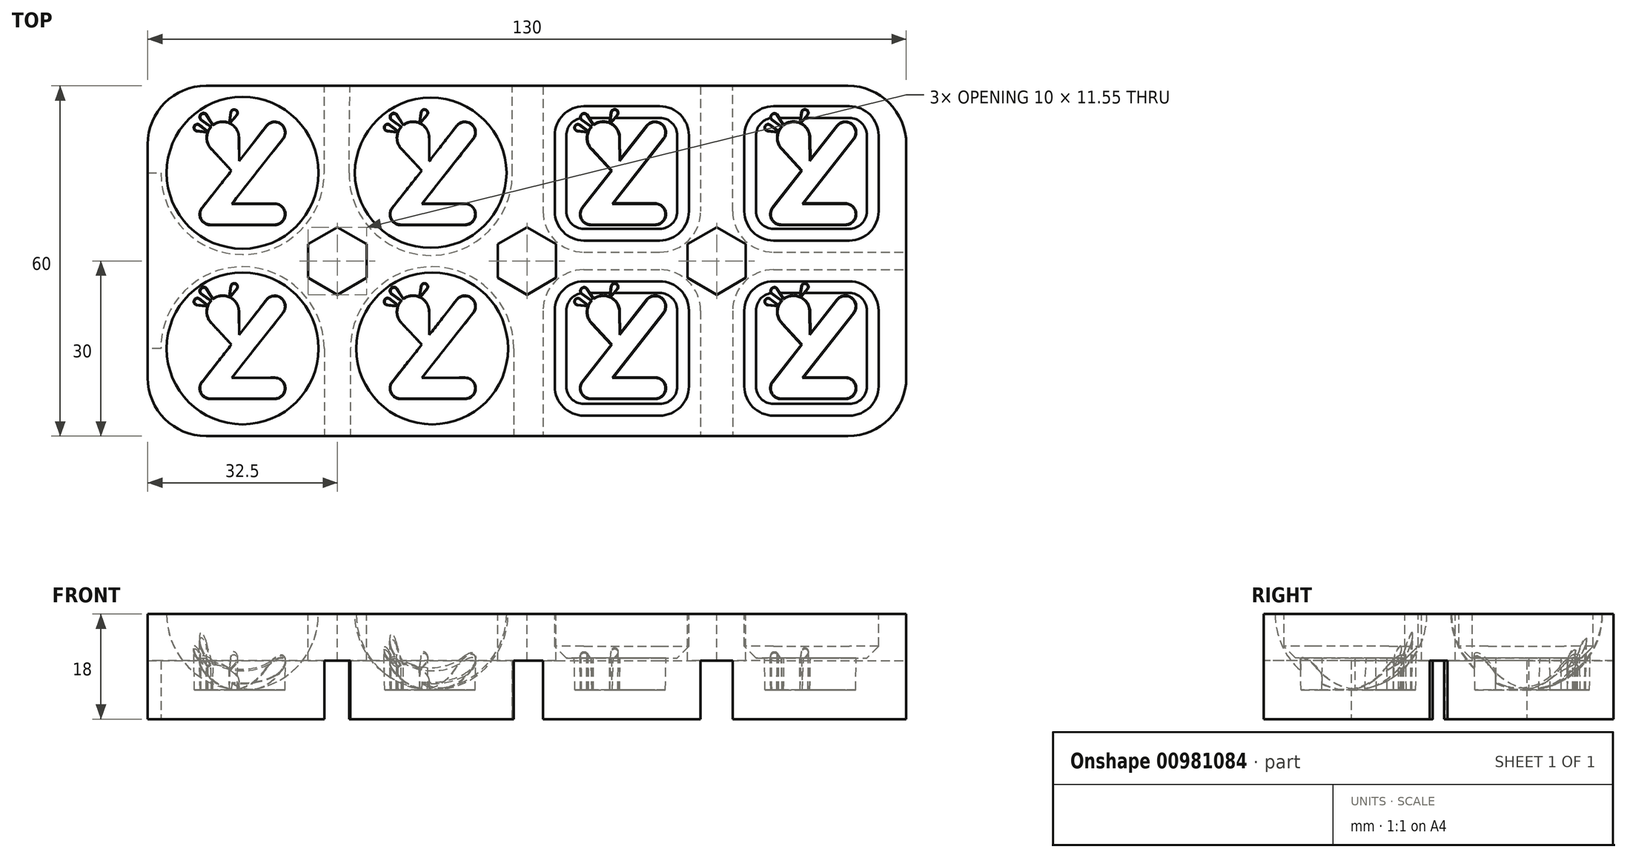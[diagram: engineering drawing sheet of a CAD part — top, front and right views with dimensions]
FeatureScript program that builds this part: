
annotation { "Feature Type Name" : "Feature", "Feature Type Description" : "" }
export const myFeature = defineFeature(function(context is Context, id is Id, definition is map)
    precondition{}
    {
        {
            var Q0;
            Q0=qCreatedBy(makeId("Top.planeOp"),FACE);
            var sketch = newSketch(context, id + "F0", { "sketchPlane" : qUnion([Q0])});
            skLineSegment(sketch, "E0.bottom", {"start": v(-55, 30) * mm, "end": v(55, 30) * mm});
            skLineSegment(sketch, "E0.top", {"start": v(-55, -30) * mm, "end": v(55, -30) * mm});
            skLineSegment(sketch, "E0.left", {"start": v(-65, 20) * mm, "end": v(-65, -20) * mm});
            skLineSegment(sketch, "E0.right", {"start": v(65, 20) * mm, "end": v(65, -20) * mm});
            skPoint(sketch, "E1", {"position": v(0, 30) * mm});
            skPoint(sketch, "E2", {"position": v(65, 0) * mm});
            skPoint(sketch, "E3.visualSharp", {"position": v(65, 30) * mm});
            skArc(sketch, "E3.filletArc", {"start": v(65, 20) * mm, "mid": v(62.07, 27.07) * mm, "end": v(55, 30) * mm});
            skPoint(sketch, "E4.visualSharp", {"position": v(65, -30) * mm});
            skArc(sketch, "E4.filletArc", {"start": v(55, -30) * mm, "mid": v(62.07, -27.07) * mm, "end": v(65, -20) * mm});
            skPoint(sketch, "E5.visualSharp", {"position": v(-65, -30) * mm});
            skArc(sketch, "E5.filletArc", {"start": v(-65, -20) * mm, "mid": v(-62.07, -27.07) * mm, "end": v(-55, -30) * mm});
            skPoint(sketch, "E6.visualSharp", {"position": v(-65, 30) * mm});
            skArc(sketch, "E6.filletArc", {"start": v(-55, 30) * mm, "mid": v(-62.07, 27.07) * mm, "end": v(-65, 20) * mm});
            skSolve(sketch);
        }
        {
            var Q0;
            Q0 = qSketchRegion(id + "F0", true);
            extrude(context, id + "F1", {"entities" : qUnion([Q0]), "depth" : 18 * mm, "offsetDistance" : 25 * mm});
        }
        {
            var Q0;
            Q0=makeQuery(id+"F1.opExtrude","CAP_FACE",FACE,{"disambiguationData":[OSD([sQuery(id+"F0.wireOp",EDGE,"E0.bottom"),sQuery(id+"F0.wireOp",EDGE,"E0.top"),sQuery(id+"F0.wireOp",EDGE,"E0.left"),sQuery(id+"F0.wireOp",EDGE,"E0.right"),sQuery(id+"F0.wireOp",EDGE,"E3.filletArc"),sQuery(id+"F0.wireOp",EDGE,"E4.filletArc"),sQuery(id+"F0.wireOp",EDGE,"E5.filletArc"),sQuery(id+"F0.wireOp",EDGE,"E6.filletArc")])],"isStart":false});
            var sketch = newSketch(context, id + "F2", { "sketchPlane" : qUnion([Q0])});
            skLineSegment(sketch, "E7", {"start": v(-65, 0) * mm, "end": v(65, 0) * mm, "construction": true});
            skLineSegment(sketch, "E8", {"start": v(0, 30) * mm, "end": v(0, -30) * mm, "construction": true});
            skLineSegment(sketch, "E9", {"start": v(-65, 20) * mm, "end": v(0, 20) * mm, "construction": true});
            skLineSegment(sketch, "E10", {"start": v(-32.5, 30) * mm, "end": v(-32.5, -30) * mm, "construction": true});
            skPoint(sketch, "E10.startSnap0", {"position": v(-32.5, 20) * mm});
            skLineSegment(sketch, "E11", {"start": v(-32.5, 30) * mm, "end": v(-32.5, 0) * mm});
            skPoint(sketch, "E12.startSnap0", {"position": v(-32.5, 15) * mm});
            skCircle(sketch, "E13", {"center": v(-48.75, 15) * mm, "radius": 12.5 * mm, "construction": true});
            skLineSegment(sketch, "E14", {"start": v(-65, 15) * mm, "end": v(-32.5, 15) * mm, "construction": true});
            skLineSegment(sketch, "E15", {"start": v(-61.25, 0) * mm, "end": v(-61.25, 15) * mm, "construction": true});
            skCircle(sketch, "E16.MirrorC", {"center": v(-73.75, 15) * mm, "radius": 12.5 * mm, "construction": true});
            skLineSegment(sketch, "E17", {"start": v(-79.25, 8) * mm, "end": v(-68.25, 8) * mm, "construction": true});
            skLineSegment(sketch, "E18", {"start": v(-68.25, 8) * mm, "end": v(-79.25, 22) * mm, "construction": true});
            skPoint(sketch, "E19", {"position": v(-73.75, 8) * mm});
            skLineSegment(sketch, "E20", {"start": v(-77.68, 23.24) * mm, "end": v(-80.82, 20.76) * mm, "construction": true});
            skLineSegment(sketch, "E21", {"start": v(-80.82, 20.76) * mm, "end": v(-72.36, 10) * mm, "construction": true});
            skLineSegment(sketch, "E22", {"start": v(-72.36, 10) * mm, "end": v(-79.25, 10) * mm, "construction": true});
            skArc(sketch, "E23", {"start": v(-68.25, 6) * mm, "mid": v(-66.45, 7.13) * mm, "end": v(-66.68, 9.24) * mm, "construction": true});
            skLineSegment(sketch, "E24", {"start": v(-79.25, 6) * mm, "end": v(-68.25, 6) * mm, "construction": true});
            skLineSegment(sketch, "E25", {"start": v(-73.13, 14.21) * mm, "end": v(-70.01, 22) * mm, "construction": true});
            skArc(sketch, "E26", {"start": v(-69.08, 21.63) * mm, "mid": v(-69.64, 22.93) * mm, "end": v(-70.94, 22.37) * mm, "construction": true});
            skLineSegment(sketch, "E27", {"start": v(-72.99, 17.27) * mm, "end": v(-71.56, 15.45) * mm, "construction": true});
            skLineSegment(sketch, "E28", {"start": v(-71.56, 15.45) * mm, "end": v(-66.68, 9.24) * mm, "construction": true});
            skLineSegment(sketch, "E29", {"start": v(-70.94, 22.37) * mm, "end": v(-72.99, 17.27) * mm, "construction": true});
            skLineSegment(sketch, "E30", {"start": v(-69.08, 21.63) * mm, "end": v(-71.56, 15.45) * mm, "construction": true});
            skLineSegment(sketch, "E31", {"start": v(-70.94, 22.37) * mm, "end": v(-69.08, 21.63) * mm, "construction": true});
            skLineSegment(sketch, "E32", {"start": v(-71.56, 15.45) * mm, "end": v(-68.3, 18.97) * mm, "construction": true});
            skPoint(sketch, "E32.endSnap0", {"position": v(-72.27, 16.36) * mm});
            skArc(sketch, "E33", {"start": v(-68.3, 18.97) * mm, "mid": v(-67.51, 20.33) * mm, "end": v(-67.54, 21.9) * mm, "construction": true});
            skLineSegment(sketch, "E34", {"start": v(-73.35, 21) * mm, "end": v(-68.3, 18.97) * mm, "construction": true});
            skLineSegment(sketch, "E35", {"start": v(-73.35, 21) * mm, "end": v(-73.4, 17.78) * mm, "construction": true});
            skLineSegment(sketch, "E36", {"start": v(-73.4, 17.78) * mm, "end": v(-72.99, 17.27) * mm, "construction": true});
            skLineSegment(sketch, "E37", {"start": v(-73.4, 17.78) * mm, "end": v(-76.54, 15.31) * mm, "construction": true});
            skLineSegment(sketch, "E38", {"start": v(-73.4, 17.78) * mm, "end": v(-77.68, 23.24) * mm, "construction": true});
            skArc(sketch, "E39", {"start": v(-77.68, 23.24) * mm, "mid": v(-80.49, 23.57) * mm, "end": v(-80.82, 20.76) * mm, "construction": true});
            skLineSegment(sketch, "E40", {"start": v(-80.82, 20.76) * mm, "end": v(-77.68, 23.24) * mm, "construction": true});
            skLineSegment(sketch, "E41", {"start": v(-80.82, 20.76) * mm, "end": v(-76.54, 15.31) * mm, "construction": true});
            skLineSegment(sketch, "E42", {"start": v(-76.54, 15.31) * mm, "end": v(-72.36, 10) * mm, "construction": true});
            skLineSegment(sketch, "E43", {"start": v(-71.87, 23.63) * mm, "end": v(-72.9, 24.88) * mm, "construction": true});
            skLineSegment(sketch, "E44", {"start": v(-71.33, 23.88) * mm, "end": v(-71.58, 25.47) * mm, "construction": true});
            skArc(sketch, "E45", {"start": v(-71.58, 25.47) * mm, "mid": v(-72.63, 26.04) * mm, "end": v(-72.9, 24.88) * mm, "construction": true});
            skLineSegment(sketch, "E46", {"start": v(-72.32, 25.35) * mm, "end": v(-70.38, 21.07) * mm, "construction": true});
            skPoint(sketch, "E47", {"position": v(-71.6, 23.77) * mm});
            skLineSegment(sketch, "E48", {"start": v(-72.9, 24.88) * mm, "end": v(-71.58, 25.47) * mm, "construction": true});
            skLineSegment(sketch, "E49.MirrorCS", {"start": v(-65.94, 22.08) * mm, "end": v(-66.48, 23.43) * mm, "construction": true});
            skLineSegment(sketch, "E50.MirrorCS", {"start": v(-66.02, 22.83) * mm, "end": v(-70.38, 21.07) * mm, "construction": true});
            skLineSegment(sketch, "E51.MirrorCS", {"start": v(-67.76, 22.45) * mm, "end": v(-66.48, 23.43) * mm, "construction": true});
            skLineSegment(sketch, "E52.MirrorCS", {"start": v(-67.54, 21.9) * mm, "end": v(-65.94, 22.08) * mm, "construction": true});
            skArc(sketch, "E53.MirrorCS", {"start": v(-66.48, 23.43) * mm, "mid": v(-65.33, 23.1) * mm, "end": v(-65.94, 22.08) * mm, "construction": true});
            skArc(sketch, "E54", {"start": v(-71.87, 23.63) * mm, "mid": v(-72.97, 22.52) * mm, "end": v(-73.35, 21) * mm, "construction": true});
            skArc(sketch, "E55", {"start": v(-71.33, 23.88) * mm, "mid": v(-71.6, 23.77) * mm, "end": v(-71.87, 23.63) * mm, "construction": true});
            skArc(sketch, "E56", {"start": v(-68.74, 23.54) * mm, "mid": v(-70, 24) * mm, "end": v(-71.33, 23.88) * mm, "construction": true});
            skArc(sketch, "E57", {"start": v(-68.08, 22.94) * mm, "mid": v(-68.39, 23.26) * mm, "end": v(-68.74, 23.54) * mm, "construction": true});
            skArc(sketch, "E58", {"start": v(-67.76, 22.45) * mm, "mid": v(-67.9, 22.7) * mm, "end": v(-68.08, 22.94) * mm, "construction": true});
            skArc(sketch, "E59", {"start": v(-67.54, 21.9) * mm, "mid": v(-67.63, 22.18) * mm, "end": v(-67.76, 22.45) * mm, "construction": true});
            skArc(sketch, "E60", {"start": v(-79.25, 10) * mm, "mid": v(-81.25, 8) * mm, "end": v(-79.25, 6) * mm, "construction": true});
            skLineSegment(sketch, "E61", {"start": v(-70.01, 22) * mm, "end": v(-66.8, 24.9) * mm, "construction": true});
            skPoint(sketch, "E62", {"position": v(-68.5, 23.36) * mm});
            skArc(sketch, "E63", {"start": v(-66.5, 24.1) * mm, "mid": v(-66.56, 25.22) * mm, "end": v(-67.69, 25.17) * mm, "construction": true});
            skLineSegment(sketch, "E64", {"start": v(-68.74, 23.54) * mm, "end": v(-68.08, 22.94) * mm, "construction": true});
            skLineSegment(sketch, "E65", {"start": v(-67.69, 25.17) * mm, "end": v(-66.5, 24.1) * mm, "construction": true});
            skLineSegment(sketch, "E66", {"start": v(-68.74, 23.54) * mm, "end": v(-67.69, 25.17) * mm, "construction": true});
            skLineSegment(sketch, "E67", {"start": v(-66.5, 24.1) * mm, "end": v(-68.08, 22.94) * mm, "construction": true});
            skLineSegment(sketch, "E68.MirrorCS", {"start": v(-51.56, 22.37) * mm, "end": v(-53.42, 21.63) * mm, "construction": true});
            skArc(sketch, "E69.MirrorCS", {"start": v(-51.17, 23.88) * mm, "mid": v(-50.9, 23.77) * mm, "end": v(-50.63, 23.63) * mm, "construction": true});
            skLineSegment(sketch, "E70.MirrorCS", {"start": v(-50.18, 25.35) * mm, "end": v(-52.12, 21.07) * mm, "construction": true});
            skLineSegment(sketch, "E71.MirrorCS", {"start": v(-51.17, 23.88) * mm, "end": v(-50.92, 25.47) * mm});
            skLineSegment(sketch, "E72.MirrorCS", {"start": v(-49.6, 24.88) * mm, "end": v(-50.92, 25.47) * mm, "construction": true});
            skLineSegment(sketch, "E73.MirrorCS", {"start": v(-54.74, 22.45) * mm, "end": v(-56.02, 23.43) * mm});
            skArc(sketch, "E74.MirrorCS", {"start": v(-54.42, 22.94) * mm, "mid": v(-54.11, 23.26) * mm, "end": v(-53.76, 23.54) * mm, "construction": true});
            skLineSegment(sketch, "E75.MirrorCS", {"start": v(-54.96, 21.9) * mm, "end": v(-56.56, 22.08) * mm});
            skLineSegment(sketch, "E76.MirrorCS", {"start": v(-53.76, 23.54) * mm, "end": v(-54.81, 25.17) * mm});
            skArc(sketch, "E77.MirrorCS", {"start": v(-54.74, 22.45) * mm, "mid": v(-54.6, 22.7) * mm, "end": v(-54.42, 22.94) * mm});
            skArc(sketch, "E78.MirrorCS", {"start": v(-50.92, 25.47) * mm, "mid": v(-49.87, 26.04) * mm, "end": v(-49.6, 24.88) * mm});
            skLineSegment(sketch, "E79.MirrorCS", {"start": v(-44.82, 23.24) * mm, "end": v(-41.68, 20.76) * mm, "construction": true});
            skArc(sketch, "E80.MirrorCS", {"start": v(-53.76, 23.54) * mm, "mid": v(-52.5, 24) * mm, "end": v(-51.17, 23.88) * mm});
            skLineSegment(sketch, "E81.MirrorCS", {"start": v(-56, 24.1) * mm, "end": v(-54.42, 22.94) * mm});
            skArc(sketch, "E82.MirrorCS", {"start": v(-54.96, 21.9) * mm, "mid": v(-54.87, 22.18) * mm, "end": v(-54.74, 22.45) * mm, "construction": true});
            skLineSegment(sketch, "E83.MirrorCS", {"start": v(-49.51, 17.27) * mm, "end": v(-50.94, 15.45) * mm, "construction": true});
            skLineSegment(sketch, "E84.MirrorCS", {"start": v(-50.63, 23.63) * mm, "end": v(-49.6, 24.88) * mm});
            skLineSegment(sketch, "E85.MirrorCS", {"start": v(-53.76, 23.54) * mm, "end": v(-54.42, 22.94) * mm, "construction": true});
            skArc(sketch, "E86.MirrorCS", {"start": v(-53.42, 21.63) * mm, "mid": v(-52.86, 22.93) * mm, "end": v(-51.56, 22.37) * mm, "construction": true});
            skLineSegment(sketch, "E87.MirrorCS", {"start": v(-56.48, 22.83) * mm, "end": v(-52.12, 21.07) * mm, "construction": true});
            skArc(sketch, "E88.MirrorCS", {"start": v(-56.02, 23.43) * mm, "mid": v(-57.17, 23.1) * mm, "end": v(-56.56, 22.08) * mm});
            skLineSegment(sketch, "E89.MirrorCS", {"start": v(-56.56, 22.08) * mm, "end": v(-56.02, 23.43) * mm, "construction": true});
            skLineSegment(sketch, "E90.MirrorCS", {"start": v(-41.68, 20.76) * mm, "end": v(-44.82, 23.24) * mm, "construction": true});
            skLineSegment(sketch, "E91.MirrorCS", {"start": v(-49.1, 17.78) * mm, "end": v(-49.51, 17.27) * mm, "construction": true});
            skLineSegment(sketch, "E92.MirrorCS", {"start": v(-54.81, 25.17) * mm, "end": v(-56, 24.1) * mm, "construction": true});
            skLineSegment(sketch, "E93.MirrorCS", {"start": v(-49.1, 17.78) * mm, "end": v(-45.96, 15.31) * mm, "construction": true});
            skLineSegment(sketch, "E94.MirrorCS", {"start": v(-52.49, 22) * mm, "end": v(-55.7, 24.9) * mm, "construction": true});
            skLineSegment(sketch, "E95.MirrorCS", {"start": v(-49.15, 21) * mm, "end": v(-49.1, 17.78) * mm});
            skArc(sketch, "E96.MirrorCS", {"start": v(-50.63, 23.63) * mm, "mid": v(-49.53, 22.52) * mm, "end": v(-49.15, 21) * mm});
            skLineSegment(sketch, "E97.MirrorCS", {"start": v(-51.56, 22.37) * mm, "end": v(-49.51, 17.27) * mm, "construction": true});
            skArc(sketch, "E98.MirrorCS", {"start": v(-54.2, 18.97) * mm, "mid": v(-54.99, 20.33) * mm, "end": v(-54.96, 21.9) * mm});
            skArc(sketch, "E99.MirrorCS", {"start": v(-56, 24.1) * mm, "mid": v(-55.94, 25.22) * mm, "end": v(-54.81, 25.17) * mm});
            skPoint(sketch, "E100.MirrorP", {"position": v(-50.9, 23.77) * mm});
            skLineSegment(sketch, "E101.MirrorCS", {"start": v(-41.68, 20.76) * mm, "end": v(-45.96, 15.31) * mm});
            skLineSegment(sketch, "E102.MirrorCS", {"start": v(-45.96, 15.31) * mm, "end": v(-50.14, 10) * mm});
            skLineSegment(sketch, "E103.MirrorCS", {"start": v(-49.15, 21) * mm, "end": v(-54.2, 18.97) * mm, "construction": true});
            skLineSegment(sketch, "E104.MirrorCS", {"start": v(-53.42, 21.63) * mm, "end": v(-50.94, 15.45) * mm, "construction": true});
            skLineSegment(sketch, "E105.MirrorCS", {"start": v(-50.94, 15.45) * mm, "end": v(-55.82, 9.24) * mm});
            skLineSegment(sketch, "E106.MirrorCS", {"start": v(-50.94, 15.45) * mm, "end": v(-54.2, 18.97) * mm});
            skLineSegment(sketch, "E107.MirrorCS", {"start": v(-41.68, 20.76) * mm, "end": v(-50.14, 10) * mm, "construction": true});
            skArc(sketch, "E108.MirrorCS", {"start": v(-43.25, 10) * mm, "mid": v(-41.25, 8) * mm, "end": v(-43.25, 6) * mm});
            skPoint(sketch, "E109.MirrorP", {"position": v(-50.23, 16.36) * mm});
            skArc(sketch, "E110.MirrorCS", {"start": v(-54.25, 6) * mm, "mid": v(-56.05, 7.13) * mm, "end": v(-55.82, 9.24) * mm});
            skLineSegment(sketch, "E111.MirrorCS", {"start": v(-54.25, 8) * mm, "end": v(-43.25, 22) * mm, "construction": true});
            skLineSegment(sketch, "E112.MirrorCS", {"start": v(-49.1, 17.78) * mm, "end": v(-44.82, 23.24) * mm});
            skPoint(sketch, "E113.MirrorP", {"position": v(-54, 23.36) * mm});
            skLineSegment(sketch, "E114.MirrorCS", {"start": v(-43.25, 6) * mm, "end": v(-54.25, 6) * mm});
            skPoint(sketch, "E115.MirrorP", {"position": v(-48.75, 8) * mm});
            skLineSegment(sketch, "E116.MirrorCS", {"start": v(-49.37, 14.21) * mm, "end": v(-52.49, 22) * mm, "construction": true});
            skArc(sketch, "E117.MirrorCS", {"start": v(-44.82, 23.24) * mm, "mid": v(-42.01, 23.57) * mm, "end": v(-41.68, 20.76) * mm});
            skLineSegment(sketch, "E118.MirrorCS", {"start": v(-50.14, 10) * mm, "end": v(-43.25, 10) * mm});
            skLineSegment(sketch, "E119.MirrorCS", {"start": v(-43.25, 8) * mm, "end": v(-54.25, 8) * mm, "construction": true});
            skLineSegment(sketch, "E120.0.1.0", {"start": v(-54.25, -21.8) * mm, "end": v(-43.25, -7.8) * mm, "construction": true});
            skLineSegment(sketch, "E120.0.1.1", {"start": v(-50.94, -14.35) * mm, "end": v(-55.82, -20.56) * mm});
            skPoint(sketch, "E120.0.1.2", {"position": v(-50.9, -6.03) * mm});
            skPoint(sketch, "E120.0.1.3", {"position": v(-50.23, -13.44) * mm});
            skArc(sketch, "E120.0.1.4", {"start": v(-44.82, -6.56) * mm, "mid": v(-42.01, -6.23) * mm, "end": v(-41.68, -9.04) * mm});
            skPoint(sketch, "E120.0.1.5", {"position": v(-48.75, -21.8) * mm});
            skLineSegment(sketch, "E120.0.1.6", {"start": v(-41.68, -9.04) * mm, "end": v(-50.14, -19.8) * mm, "construction": true});
            skPoint(sketch, "E120.0.1.7", {"position": v(-48.75, -14.8) * mm});
            skArc(sketch, "E120.0.1.8", {"start": v(-43.25, -19.8) * mm, "mid": v(-41.25, -21.8) * mm, "end": v(-43.25, -23.8) * mm});
            skPoint(sketch, "E120.0.1.9", {"position": v(-54, -6.44) * mm});
            skLineSegment(sketch, "E120.0.1.10", {"start": v(-49.1, -12.02) * mm, "end": v(-44.82, -6.56) * mm});
            skLineSegment(sketch, "E120.0.1.11", {"start": v(-41.68, -9.04) * mm, "end": v(-45.96, -14.49) * mm});
            skLineSegment(sketch, "E120.0.1.12", {"start": v(-43.25, -21.8) * mm, "end": v(-54.25, -21.8) * mm, "construction": true});
            skLineSegment(sketch, "E120.0.1.13", {"start": v(-43.25, -23.8) * mm, "end": v(-54.25, -23.8) * mm});
            skLineSegment(sketch, "E120.0.1.14", {"start": v(-50.14, -19.8) * mm, "end": v(-43.25, -19.8) * mm});
            skLineSegment(sketch, "E120.0.1.15", {"start": v(-45.96, -14.49) * mm, "end": v(-50.14, -19.8) * mm});
            skArc(sketch, "E120.0.1.16", {"start": v(-54.25, -23.8) * mm, "mid": v(-56.05, -22.67) * mm, "end": v(-55.82, -20.56) * mm});
            skLineSegment(sketch, "E120.0.1.17", {"start": v(-50.94, -14.35) * mm, "end": v(-54.2, -10.83) * mm});
            skLineSegment(sketch, "E120.0.1.18", {"start": v(-49.15, -8.8) * mm, "end": v(-54.2, -10.83) * mm, "construction": true});
            skLineSegment(sketch, "E120.0.1.19", {"start": v(-49.1, -12.02) * mm, "end": v(-45.96, -14.49) * mm, "construction": true});
            skLineSegment(sketch, "E120.0.1.20", {"start": v(-53.42, -8.17) * mm, "end": v(-50.94, -14.35) * mm, "construction": true});
            skArc(sketch, "E120.0.1.21", {"start": v(-54.2, -10.83) * mm, "mid": v(-54.99, -9.47) * mm, "end": v(-54.96, -7.9) * mm});
            skArc(sketch, "E120.0.1.22", {"start": v(-56, -5.7) * mm, "mid": v(-55.94, -4.58) * mm, "end": v(-54.81, -4.63) * mm});
            skArc(sketch, "E120.0.1.23", {"start": v(-56.02, -6.37) * mm, "mid": v(-57.17, -6.7) * mm, "end": v(-56.56, -7.72) * mm});
            skLineSegment(sketch, "E120.0.1.24", {"start": v(-49.15, -8.8) * mm, "end": v(-49.1, -12.02) * mm});
            skLineSegment(sketch, "E120.0.1.25", {"start": v(-44.82, -6.56) * mm, "end": v(-41.68, -9.04) * mm, "construction": true});
            skLineSegment(sketch, "E120.0.1.26", {"start": v(-51.56, -7.43) * mm, "end": v(-49.51, -12.53) * mm, "construction": true});
            skLineSegment(sketch, "E120.0.1.27", {"start": v(-49.37, -15.59) * mm, "end": v(-52.49, -7.8) * mm, "construction": true});
            skArc(sketch, "E120.0.1.28", {"start": v(-50.63, -6.17) * mm, "mid": v(-49.53, -7.28) * mm, "end": v(-49.15, -8.8) * mm});
            skLineSegment(sketch, "E120.0.1.29", {"start": v(-49.51, -12.53) * mm, "end": v(-50.94, -14.35) * mm, "construction": true});
            skLineSegment(sketch, "E120.0.1.30", {"start": v(-41.68, -9.04) * mm, "end": v(-44.82, -6.56) * mm, "construction": true});
            skLineSegment(sketch, "E120.0.1.31", {"start": v(-49.1, -12.02) * mm, "end": v(-49.51, -12.53) * mm, "construction": true});
            skLineSegment(sketch, "E120.0.1.32", {"start": v(-53.76, -6.26) * mm, "end": v(-54.81, -4.63) * mm});
            skLineSegment(sketch, "E120.0.1.33", {"start": v(-54.81, -4.63) * mm, "end": v(-56, -5.7) * mm, "construction": true});
            skLineSegment(sketch, "E120.0.1.34", {"start": v(-52.49, -7.8) * mm, "end": v(-55.7, -4.9) * mm, "construction": true});
            skLineSegment(sketch, "E120.0.1.35", {"start": v(-50.63, -6.17) * mm, "end": v(-49.6, -4.92) * mm});
            skLineSegment(sketch, "E120.0.1.36", {"start": v(-49.6, -4.92) * mm, "end": v(-50.92, -4.33) * mm, "construction": true});
            skLineSegment(sketch, "E120.0.1.37", {"start": v(-50.18, -4.45) * mm, "end": v(-52.12, -8.73) * mm, "construction": true});
            skLineSegment(sketch, "E120.0.1.38", {"start": v(-51.17, -5.92) * mm, "end": v(-50.92, -4.33) * mm});
            skArc(sketch, "E120.0.1.39", {"start": v(-51.17, -5.92) * mm, "mid": v(-50.9, -6.03) * mm, "end": v(-50.63, -6.17) * mm, "construction": true});
            skArc(sketch, "E120.0.1.40", {"start": v(-53.76, -6.26) * mm, "mid": v(-52.5, -5.8) * mm, "end": v(-51.17, -5.92) * mm});
            skArc(sketch, "E120.0.1.41", {"start": v(-50.92, -4.33) * mm, "mid": v(-49.87, -3.76) * mm, "end": v(-49.6, -4.92) * mm});
            skLineSegment(sketch, "E120.0.1.42", {"start": v(-56, -5.7) * mm, "end": v(-54.42, -6.86) * mm});
            skLineSegment(sketch, "E120.0.1.43", {"start": v(-51.56, -7.43) * mm, "end": v(-53.42, -8.17) * mm, "construction": true});
            skLineSegment(sketch, "E120.0.1.44", {"start": v(-56.56, -7.72) * mm, "end": v(-56.02, -6.37) * mm, "construction": true});
            skArc(sketch, "E120.0.1.45", {"start": v(-53.42, -8.17) * mm, "mid": v(-52.86, -6.87) * mm, "end": v(-51.56, -7.43) * mm, "construction": true});
            skLineSegment(sketch, "E120.0.1.46", {"start": v(-56.48, -6.97) * mm, "end": v(-52.12, -8.73) * mm, "construction": true});
            skLineSegment(sketch, "E120.0.1.47", {"start": v(-53.76, -6.26) * mm, "end": v(-54.42, -6.86) * mm, "construction": true});
            skLineSegment(sketch, "E120.0.1.48", {"start": v(-54.96, -7.9) * mm, "end": v(-56.56, -7.72) * mm});
            skArc(sketch, "E120.0.1.49", {"start": v(-54.96, -7.9) * mm, "mid": v(-54.87, -7.62) * mm, "end": v(-54.74, -7.35) * mm, "construction": true});
            skLineSegment(sketch, "E120.0.1.50", {"start": v(-54.74, -7.35) * mm, "end": v(-56.02, -6.37) * mm});
            skArc(sketch, "E120.0.1.51", {"start": v(-54.42, -6.86) * mm, "mid": v(-54.11, -6.54) * mm, "end": v(-53.76, -6.26) * mm, "construction": true});
            skArc(sketch, "E120.0.1.52", {"start": v(-54.74, -7.35) * mm, "mid": v(-54.6, -7.1) * mm, "end": v(-54.42, -6.86) * mm});
            skLineSegment(sketch, "E120.1.0.0", {"start": v(-21.65, 8) * mm, "end": v(-10.65, 22) * mm, "construction": true});
            skLineSegment(sketch, "E120.1.0.1", {"start": v(-18.34, 15.45) * mm, "end": v(-23.22, 9.24) * mm});
            skPoint(sketch, "E120.1.0.2", {"position": v(-18.3, 23.77) * mm});
            skPoint(sketch, "E120.1.0.3", {"position": v(-17.63, 16.36) * mm});
            skArc(sketch, "E120.1.0.4", {"start": v(-12.22, 23.24) * mm, "mid": v(-9.41, 23.57) * mm, "end": v(-9.08, 20.76) * mm});
            skPoint(sketch, "E120.1.0.5", {"position": v(-16.15, 8) * mm});
            skLineSegment(sketch, "E120.1.0.6", {"start": v(-9.08, 20.76) * mm, "end": v(-17.54, 10) * mm, "construction": true});
            skPoint(sketch, "E120.1.0.7", {"position": v(-16.15, 15) * mm});
            skArc(sketch, "E120.1.0.8", {"start": v(-10.65, 10) * mm, "mid": v(-8.65, 8) * mm, "end": v(-10.65, 6) * mm});
            skPoint(sketch, "E120.1.0.9", {"position": v(-21.4, 23.36) * mm});
            skLineSegment(sketch, "E120.1.0.10", {"start": v(-16.5, 17.78) * mm, "end": v(-12.22, 23.24) * mm});
            skLineSegment(sketch, "E120.1.0.11", {"start": v(-9.08, 20.76) * mm, "end": v(-13.36, 15.31) * mm});
            skLineSegment(sketch, "E120.1.0.12", {"start": v(-10.65, 8) * mm, "end": v(-21.65, 8) * mm, "construction": true});
            skLineSegment(sketch, "E120.1.0.13", {"start": v(-10.65, 6) * mm, "end": v(-21.65, 6) * mm});
            skLineSegment(sketch, "E120.1.0.14", {"start": v(-17.54, 10) * mm, "end": v(-10.65, 10) * mm});
            skLineSegment(sketch, "E120.1.0.15", {"start": v(-13.36, 15.31) * mm, "end": v(-17.54, 10) * mm});
            skArc(sketch, "E120.1.0.16", {"start": v(-21.65, 6) * mm, "mid": v(-23.45, 7.13) * mm, "end": v(-23.22, 9.24) * mm});
            skLineSegment(sketch, "E120.1.0.17", {"start": v(-18.34, 15.45) * mm, "end": v(-21.6, 18.97) * mm});
            skLineSegment(sketch, "E120.1.0.18", {"start": v(-16.55, 21) * mm, "end": v(-21.6, 18.97) * mm, "construction": true});
            skLineSegment(sketch, "E120.1.0.19", {"start": v(-16.5, 17.78) * mm, "end": v(-13.36, 15.31) * mm, "construction": true});
            skLineSegment(sketch, "E120.1.0.20", {"start": v(-20.82, 21.63) * mm, "end": v(-18.34, 15.45) * mm, "construction": true});
            skArc(sketch, "E120.1.0.21", {"start": v(-21.6, 18.97) * mm, "mid": v(-22.39, 20.33) * mm, "end": v(-22.36, 21.9) * mm});
            skArc(sketch, "E120.1.0.22", {"start": v(-23.4, 24.1) * mm, "mid": v(-23.34, 25.22) * mm, "end": v(-22.21, 25.17) * mm});
            skArc(sketch, "E120.1.0.23", {"start": v(-23.42, 23.43) * mm, "mid": v(-24.57, 23.1) * mm, "end": v(-23.96, 22.08) * mm});
            skLineSegment(sketch, "E120.1.0.24", {"start": v(-16.55, 21) * mm, "end": v(-16.5, 17.78) * mm});
            skLineSegment(sketch, "E120.1.0.25", {"start": v(-12.22, 23.24) * mm, "end": v(-9.08, 20.76) * mm, "construction": true});
            skLineSegment(sketch, "E120.1.0.26", {"start": v(-18.96, 22.37) * mm, "end": v(-16.91, 17.27) * mm, "construction": true});
            skLineSegment(sketch, "E120.1.0.27", {"start": v(-16.77, 14.21) * mm, "end": v(-19.89, 22) * mm, "construction": true});
            skArc(sketch, "E120.1.0.28", {"start": v(-18.03, 23.63) * mm, "mid": v(-16.93, 22.52) * mm, "end": v(-16.55, 21) * mm});
            skLineSegment(sketch, "E120.1.0.29", {"start": v(-16.91, 17.27) * mm, "end": v(-18.34, 15.45) * mm, "construction": true});
            skLineSegment(sketch, "E120.1.0.30", {"start": v(-9.08, 20.76) * mm, "end": v(-12.22, 23.24) * mm, "construction": true});
            skLineSegment(sketch, "E120.1.0.31", {"start": v(-16.5, 17.78) * mm, "end": v(-16.91, 17.27) * mm, "construction": true});
            skLineSegment(sketch, "E120.1.0.32", {"start": v(-21.16, 23.54) * mm, "end": v(-22.21, 25.17) * mm});
            skLineSegment(sketch, "E120.1.0.33", {"start": v(-22.21, 25.17) * mm, "end": v(-23.4, 24.1) * mm, "construction": true});
            skLineSegment(sketch, "E120.1.0.34", {"start": v(-19.89, 22) * mm, "end": v(-23.1, 24.9) * mm, "construction": true});
            skLineSegment(sketch, "E120.1.0.35", {"start": v(-18.03, 23.63) * mm, "end": v(-17, 24.88) * mm});
            skLineSegment(sketch, "E120.1.0.36", {"start": v(-17, 24.88) * mm, "end": v(-18.32, 25.47) * mm, "construction": true});
            skLineSegment(sketch, "E120.1.0.37", {"start": v(-17.58, 25.35) * mm, "end": v(-19.52, 21.07) * mm, "construction": true});
            skLineSegment(sketch, "E120.1.0.38", {"start": v(-18.57, 23.88) * mm, "end": v(-18.32, 25.47) * mm});
            skArc(sketch, "E120.1.0.39", {"start": v(-18.57, 23.88) * mm, "mid": v(-18.3, 23.77) * mm, "end": v(-18.03, 23.63) * mm, "construction": true});
            skArc(sketch, "E120.1.0.40", {"start": v(-21.16, 23.54) * mm, "mid": v(-19.9, 24) * mm, "end": v(-18.57, 23.88) * mm});
            skArc(sketch, "E120.1.0.41", {"start": v(-18.32, 25.47) * mm, "mid": v(-17.27, 26.04) * mm, "end": v(-17, 24.88) * mm});
            skLineSegment(sketch, "E120.1.0.42", {"start": v(-23.4, 24.1) * mm, "end": v(-21.82, 22.94) * mm});
            skLineSegment(sketch, "E120.1.0.43", {"start": v(-18.96, 22.37) * mm, "end": v(-20.82, 21.63) * mm, "construction": true});
            skLineSegment(sketch, "E120.1.0.44", {"start": v(-23.96, 22.08) * mm, "end": v(-23.42, 23.43) * mm, "construction": true});
            skArc(sketch, "E120.1.0.45", {"start": v(-20.82, 21.63) * mm, "mid": v(-20.26, 22.93) * mm, "end": v(-18.96, 22.37) * mm, "construction": true});
            skLineSegment(sketch, "E120.1.0.46", {"start": v(-23.88, 22.83) * mm, "end": v(-19.52, 21.07) * mm, "construction": true});
            skLineSegment(sketch, "E120.1.0.47", {"start": v(-21.16, 23.54) * mm, "end": v(-21.82, 22.94) * mm, "construction": true});
            skLineSegment(sketch, "E120.1.0.48", {"start": v(-22.36, 21.9) * mm, "end": v(-23.96, 22.08) * mm});
            skArc(sketch, "E120.1.0.49", {"start": v(-22.36, 21.9) * mm, "mid": v(-22.27, 22.18) * mm, "end": v(-22.14, 22.45) * mm, "construction": true});
            skLineSegment(sketch, "E120.1.0.50", {"start": v(-22.14, 22.45) * mm, "end": v(-23.42, 23.43) * mm});
            skArc(sketch, "E120.1.0.51", {"start": v(-21.82, 22.94) * mm, "mid": v(-21.51, 23.26) * mm, "end": v(-21.16, 23.54) * mm, "construction": true});
            skArc(sketch, "E120.1.0.52", {"start": v(-22.14, 22.45) * mm, "mid": v(-22, 22.7) * mm, "end": v(-21.82, 22.94) * mm});
            skLineSegment(sketch, "E120.1.1.0", {"start": v(-21.65, -21.8) * mm, "end": v(-10.65, -7.8) * mm, "construction": true});
            skLineSegment(sketch, "E120.1.1.1", {"start": v(-18.34, -14.35) * mm, "end": v(-23.22, -20.56) * mm});
            skPoint(sketch, "E120.1.1.2", {"position": v(-18.3, -6.03) * mm});
            skPoint(sketch, "E120.1.1.3", {"position": v(-17.63, -13.44) * mm});
            skArc(sketch, "E120.1.1.4", {"start": v(-12.22, -6.56) * mm, "mid": v(-9.41, -6.23) * mm, "end": v(-9.08, -9.04) * mm});
            skPoint(sketch, "E120.1.1.5", {"position": v(-16.15, -21.8) * mm});
            skLineSegment(sketch, "E120.1.1.6", {"start": v(-9.08, -9.04) * mm, "end": v(-17.54, -19.8) * mm, "construction": true});
            skPoint(sketch, "E120.1.1.7", {"position": v(-16.15, -14.8) * mm});
            skArc(sketch, "E120.1.1.8", {"start": v(-10.65, -19.8) * mm, "mid": v(-8.65, -21.8) * mm, "end": v(-10.65, -23.8) * mm});
            skPoint(sketch, "E120.1.1.9", {"position": v(-21.4, -6.44) * mm});
            skLineSegment(sketch, "E120.1.1.10", {"start": v(-16.5, -12.02) * mm, "end": v(-12.22, -6.56) * mm});
            skLineSegment(sketch, "E120.1.1.11", {"start": v(-9.08, -9.04) * mm, "end": v(-13.36, -14.49) * mm});
            skLineSegment(sketch, "E120.1.1.12", {"start": v(-10.65, -21.8) * mm, "end": v(-21.65, -21.8) * mm, "construction": true});
            skLineSegment(sketch, "E120.1.1.13", {"start": v(-10.65, -23.8) * mm, "end": v(-21.65, -23.8) * mm});
            skLineSegment(sketch, "E120.1.1.14", {"start": v(-17.54, -19.8) * mm, "end": v(-10.65, -19.8) * mm});
            skLineSegment(sketch, "E120.1.1.15", {"start": v(-13.36, -14.49) * mm, "end": v(-17.54, -19.8) * mm});
            skArc(sketch, "E120.1.1.16", {"start": v(-21.65, -23.8) * mm, "mid": v(-23.45, -22.67) * mm, "end": v(-23.22, -20.56) * mm});
            skLineSegment(sketch, "E120.1.1.17", {"start": v(-18.34, -14.35) * mm, "end": v(-21.6, -10.83) * mm});
            skLineSegment(sketch, "E120.1.1.18", {"start": v(-16.55, -8.8) * mm, "end": v(-21.6, -10.83) * mm, "construction": true});
            skLineSegment(sketch, "E120.1.1.19", {"start": v(-16.5, -12.02) * mm, "end": v(-13.36, -14.49) * mm, "construction": true});
            skLineSegment(sketch, "E120.1.1.20", {"start": v(-20.82, -8.17) * mm, "end": v(-18.34, -14.35) * mm, "construction": true});
            skArc(sketch, "E120.1.1.21", {"start": v(-21.6, -10.83) * mm, "mid": v(-22.39, -9.47) * mm, "end": v(-22.36, -7.9) * mm});
            skArc(sketch, "E120.1.1.22", {"start": v(-23.4, -5.7) * mm, "mid": v(-23.34, -4.58) * mm, "end": v(-22.21, -4.63) * mm});
            skArc(sketch, "E120.1.1.23", {"start": v(-23.42, -6.37) * mm, "mid": v(-24.57, -6.7) * mm, "end": v(-23.96, -7.72) * mm});
            skLineSegment(sketch, "E120.1.1.24", {"start": v(-16.55, -8.8) * mm, "end": v(-16.5, -12.02) * mm});
            skLineSegment(sketch, "E120.1.1.25", {"start": v(-12.22, -6.56) * mm, "end": v(-9.08, -9.04) * mm, "construction": true});
            skLineSegment(sketch, "E120.1.1.26", {"start": v(-18.96, -7.43) * mm, "end": v(-16.91, -12.53) * mm, "construction": true});
            skLineSegment(sketch, "E120.1.1.27", {"start": v(-16.77, -15.59) * mm, "end": v(-19.89, -7.8) * mm, "construction": true});
            skArc(sketch, "E120.1.1.28", {"start": v(-18.03, -6.17) * mm, "mid": v(-16.93, -7.28) * mm, "end": v(-16.55, -8.8) * mm});
            skLineSegment(sketch, "E120.1.1.29", {"start": v(-16.91, -12.53) * mm, "end": v(-18.34, -14.35) * mm, "construction": true});
            skLineSegment(sketch, "E120.1.1.30", {"start": v(-9.08, -9.04) * mm, "end": v(-12.22, -6.56) * mm, "construction": true});
            skLineSegment(sketch, "E120.1.1.31", {"start": v(-16.5, -12.02) * mm, "end": v(-16.91, -12.53) * mm, "construction": true});
            skLineSegment(sketch, "E120.1.1.32", {"start": v(-21.16, -6.26) * mm, "end": v(-22.21, -4.63) * mm});
            skLineSegment(sketch, "E120.1.1.33", {"start": v(-22.21, -4.63) * mm, "end": v(-23.4, -5.7) * mm, "construction": true});
            skLineSegment(sketch, "E120.1.1.34", {"start": v(-19.89, -7.8) * mm, "end": v(-23.1, -4.9) * mm, "construction": true});
            skLineSegment(sketch, "E120.1.1.35", {"start": v(-18.03, -6.17) * mm, "end": v(-17, -4.92) * mm});
            skLineSegment(sketch, "E120.1.1.36", {"start": v(-17, -4.92) * mm, "end": v(-18.32, -4.33) * mm, "construction": true});
            skLineSegment(sketch, "E120.1.1.37", {"start": v(-17.58, -4.45) * mm, "end": v(-19.52, -8.73) * mm, "construction": true});
            skLineSegment(sketch, "E120.1.1.38", {"start": v(-18.57, -5.92) * mm, "end": v(-18.32, -4.33) * mm});
            skArc(sketch, "E120.1.1.39", {"start": v(-18.57, -5.92) * mm, "mid": v(-18.3, -6.03) * mm, "end": v(-18.03, -6.17) * mm, "construction": true});
            skArc(sketch, "E120.1.1.40", {"start": v(-21.16, -6.26) * mm, "mid": v(-19.9, -5.8) * mm, "end": v(-18.57, -5.92) * mm});
            skArc(sketch, "E120.1.1.41", {"start": v(-18.32, -4.33) * mm, "mid": v(-17.27, -3.76) * mm, "end": v(-17, -4.92) * mm});
            skLineSegment(sketch, "E120.1.1.42", {"start": v(-23.4, -5.7) * mm, "end": v(-21.82, -6.86) * mm});
            skLineSegment(sketch, "E120.1.1.43", {"start": v(-18.96, -7.43) * mm, "end": v(-20.82, -8.17) * mm, "construction": true});
            skLineSegment(sketch, "E120.1.1.44", {"start": v(-23.96, -7.72) * mm, "end": v(-23.42, -6.37) * mm, "construction": true});
            skArc(sketch, "E120.1.1.45", {"start": v(-20.82, -8.17) * mm, "mid": v(-20.26, -6.87) * mm, "end": v(-18.96, -7.43) * mm, "construction": true});
            skLineSegment(sketch, "E120.1.1.46", {"start": v(-23.88, -6.97) * mm, "end": v(-19.52, -8.73) * mm, "construction": true});
            skLineSegment(sketch, "E120.1.1.47", {"start": v(-21.16, -6.26) * mm, "end": v(-21.82, -6.86) * mm, "construction": true});
            skLineSegment(sketch, "E120.1.1.48", {"start": v(-22.36, -7.9) * mm, "end": v(-23.96, -7.72) * mm});
            skArc(sketch, "E120.1.1.49", {"start": v(-22.36, -7.9) * mm, "mid": v(-22.27, -7.62) * mm, "end": v(-22.14, -7.35) * mm, "construction": true});
            skLineSegment(sketch, "E120.1.1.50", {"start": v(-22.14, -7.35) * mm, "end": v(-23.42, -6.37) * mm});
            skArc(sketch, "E120.1.1.51", {"start": v(-21.82, -6.86) * mm, "mid": v(-21.51, -6.54) * mm, "end": v(-21.16, -6.26) * mm, "construction": true});
            skArc(sketch, "E120.1.1.52", {"start": v(-22.14, -7.35) * mm, "mid": v(-22, -7.1) * mm, "end": v(-21.82, -6.86) * mm});
            skLineSegment(sketch, "E120.2.0.0", {"start": v(10.95, 8) * mm, "end": v(21.95, 22) * mm, "construction": true});
            skLineSegment(sketch, "E120.2.0.1", {"start": v(14.26, 15.45) * mm, "end": v(9.38, 9.24) * mm});
            skPoint(sketch, "E120.2.0.2", {"position": v(14.3, 23.77) * mm});
            skPoint(sketch, "E120.2.0.3", {"position": v(14.97, 16.36) * mm});
            skArc(sketch, "E120.2.0.4", {"start": v(20.38, 23.24) * mm, "mid": v(23.19, 23.57) * mm, "end": v(23.52, 20.76) * mm});
            skPoint(sketch, "E120.2.0.5", {"position": v(16.45, 8) * mm});
            skLineSegment(sketch, "E120.2.0.6", {"start": v(23.52, 20.76) * mm, "end": v(15.06, 10) * mm, "construction": true});
            skPoint(sketch, "E120.2.0.7", {"position": v(16.45, 15) * mm});
            skArc(sketch, "E120.2.0.8", {"start": v(21.95, 10) * mm, "mid": v(23.95, 8) * mm, "end": v(21.95, 6) * mm});
            skPoint(sketch, "E120.2.0.9", {"position": v(11.2, 23.36) * mm});
            skLineSegment(sketch, "E120.2.0.10", {"start": v(16.1, 17.78) * mm, "end": v(20.38, 23.24) * mm});
            skLineSegment(sketch, "E120.2.0.11", {"start": v(23.52, 20.76) * mm, "end": v(19.24, 15.31) * mm});
            skLineSegment(sketch, "E120.2.0.12", {"start": v(21.95, 8) * mm, "end": v(10.95, 8) * mm, "construction": true});
            skLineSegment(sketch, "E120.2.0.13", {"start": v(21.95, 6) * mm, "end": v(10.95, 6) * mm});
            skLineSegment(sketch, "E120.2.0.14", {"start": v(15.06, 10) * mm, "end": v(21.95, 10) * mm});
            skLineSegment(sketch, "E120.2.0.15", {"start": v(19.24, 15.31) * mm, "end": v(15.06, 10) * mm});
            skArc(sketch, "E120.2.0.16", {"start": v(10.95, 6) * mm, "mid": v(9.15, 7.13) * mm, "end": v(9.38, 9.24) * mm});
            skLineSegment(sketch, "E120.2.0.17", {"start": v(14.26, 15.45) * mm, "end": v(11, 18.97) * mm});
            skLineSegment(sketch, "E120.2.0.18", {"start": v(16.05, 21) * mm, "end": v(11, 18.97) * mm, "construction": true});
            skLineSegment(sketch, "E120.2.0.19", {"start": v(16.1, 17.78) * mm, "end": v(19.24, 15.31) * mm, "construction": true});
            skLineSegment(sketch, "E120.2.0.20", {"start": v(11.78, 21.63) * mm, "end": v(14.26, 15.45) * mm, "construction": true});
            skArc(sketch, "E120.2.0.21", {"start": v(11, 18.97) * mm, "mid": v(10.21, 20.33) * mm, "end": v(10.24, 21.9) * mm});
            skArc(sketch, "E120.2.0.22", {"start": v(9.2, 24.1) * mm, "mid": v(9.26, 25.22) * mm, "end": v(10.39, 25.17) * mm});
            skArc(sketch, "E120.2.0.23", {"start": v(9.18, 23.43) * mm, "mid": v(8.03, 23.1) * mm, "end": v(8.64, 22.08) * mm});
            skLineSegment(sketch, "E120.2.0.24", {"start": v(16.05, 21) * mm, "end": v(16.1, 17.78) * mm});
            skLineSegment(sketch, "E120.2.0.25", {"start": v(20.38, 23.24) * mm, "end": v(23.52, 20.76) * mm, "construction": true});
            skLineSegment(sketch, "E120.2.0.26", {"start": v(13.64, 22.37) * mm, "end": v(15.69, 17.27) * mm, "construction": true});
            skLineSegment(sketch, "E120.2.0.27", {"start": v(15.83, 14.21) * mm, "end": v(12.71, 22) * mm, "construction": true});
            skArc(sketch, "E120.2.0.28", {"start": v(14.57, 23.63) * mm, "mid": v(15.67, 22.52) * mm, "end": v(16.05, 21) * mm});
            skLineSegment(sketch, "E120.2.0.29", {"start": v(15.69, 17.27) * mm, "end": v(14.26, 15.45) * mm, "construction": true});
            skLineSegment(sketch, "E120.2.0.30", {"start": v(23.52, 20.76) * mm, "end": v(20.38, 23.24) * mm, "construction": true});
            skLineSegment(sketch, "E120.2.0.31", {"start": v(16.1, 17.78) * mm, "end": v(15.69, 17.27) * mm, "construction": true});
            skLineSegment(sketch, "E120.2.0.32", {"start": v(11.44, 23.54) * mm, "end": v(10.39, 25.17) * mm});
            skLineSegment(sketch, "E120.2.0.33", {"start": v(10.39, 25.17) * mm, "end": v(9.2, 24.1) * mm, "construction": true});
            skLineSegment(sketch, "E120.2.0.34", {"start": v(12.71, 22) * mm, "end": v(9.5, 24.9) * mm, "construction": true});
            skLineSegment(sketch, "E120.2.0.35", {"start": v(14.57, 23.63) * mm, "end": v(15.6, 24.88) * mm});
            skLineSegment(sketch, "E120.2.0.36", {"start": v(15.6, 24.88) * mm, "end": v(14.28, 25.47) * mm, "construction": true});
            skLineSegment(sketch, "E120.2.0.37", {"start": v(15.02, 25.35) * mm, "end": v(13.08, 21.07) * mm, "construction": true});
            skLineSegment(sketch, "E120.2.0.38", {"start": v(14.03, 23.88) * mm, "end": v(14.28, 25.47) * mm});
            skArc(sketch, "E120.2.0.39", {"start": v(14.03, 23.88) * mm, "mid": v(14.3, 23.77) * mm, "end": v(14.57, 23.63) * mm, "construction": true});
            skArc(sketch, "E120.2.0.40", {"start": v(11.44, 23.54) * mm, "mid": v(12.7, 24) * mm, "end": v(14.03, 23.88) * mm});
            skArc(sketch, "E120.2.0.41", {"start": v(14.28, 25.47) * mm, "mid": v(15.33, 26.04) * mm, "end": v(15.6, 24.88) * mm});
            skLineSegment(sketch, "E120.2.0.42", {"start": v(9.2, 24.1) * mm, "end": v(10.78, 22.94) * mm});
            skLineSegment(sketch, "E120.2.0.43", {"start": v(13.64, 22.37) * mm, "end": v(11.78, 21.63) * mm, "construction": true});
            skLineSegment(sketch, "E120.2.0.44", {"start": v(8.64, 22.08) * mm, "end": v(9.18, 23.43) * mm, "construction": true});
            skArc(sketch, "E120.2.0.45", {"start": v(11.78, 21.63) * mm, "mid": v(12.34, 22.93) * mm, "end": v(13.64, 22.37) * mm, "construction": true});
            skLineSegment(sketch, "E120.2.0.46", {"start": v(8.72, 22.83) * mm, "end": v(13.08, 21.07) * mm, "construction": true});
            skLineSegment(sketch, "E120.2.0.47", {"start": v(11.44, 23.54) * mm, "end": v(10.78, 22.94) * mm, "construction": true});
            skLineSegment(sketch, "E120.2.0.48", {"start": v(10.24, 21.9) * mm, "end": v(8.64, 22.08) * mm});
            skArc(sketch, "E120.2.0.49", {"start": v(10.24, 21.9) * mm, "mid": v(10.33, 22.18) * mm, "end": v(10.46, 22.45) * mm, "construction": true});
            skLineSegment(sketch, "E120.2.0.50", {"start": v(10.46, 22.45) * mm, "end": v(9.18, 23.43) * mm});
            skArc(sketch, "E120.2.0.51", {"start": v(10.78, 22.94) * mm, "mid": v(11.09, 23.26) * mm, "end": v(11.44, 23.54) * mm, "construction": true});
            skArc(sketch, "E120.2.0.52", {"start": v(10.46, 22.45) * mm, "mid": v(10.6, 22.7) * mm, "end": v(10.78, 22.94) * mm});
            skLineSegment(sketch, "E120.2.1.0", {"start": v(10.95, -21.8) * mm, "end": v(21.95, -7.8) * mm, "construction": true});
            skLineSegment(sketch, "E120.2.1.1", {"start": v(14.26, -14.35) * mm, "end": v(9.38, -20.56) * mm});
            skPoint(sketch, "E120.2.1.2", {"position": v(14.3, -6.03) * mm});
            skPoint(sketch, "E120.2.1.3", {"position": v(14.97, -13.44) * mm});
            skArc(sketch, "E120.2.1.4", {"start": v(20.38, -6.56) * mm, "mid": v(23.19, -6.23) * mm, "end": v(23.52, -9.04) * mm});
            skPoint(sketch, "E120.2.1.5", {"position": v(16.45, -21.8) * mm});
            skLineSegment(sketch, "E120.2.1.6", {"start": v(23.52, -9.04) * mm, "end": v(15.06, -19.8) * mm, "construction": true});
            skPoint(sketch, "E120.2.1.7", {"position": v(16.45, -14.8) * mm});
            skArc(sketch, "E120.2.1.8", {"start": v(21.95, -19.8) * mm, "mid": v(23.95, -21.8) * mm, "end": v(21.95, -23.8) * mm});
            skPoint(sketch, "E120.2.1.9", {"position": v(11.2, -6.44) * mm});
            skLineSegment(sketch, "E120.2.1.10", {"start": v(16.1, -12.02) * mm, "end": v(20.38, -6.56) * mm});
            skLineSegment(sketch, "E120.2.1.11", {"start": v(23.52, -9.04) * mm, "end": v(19.24, -14.49) * mm});
            skLineSegment(sketch, "E120.2.1.12", {"start": v(21.95, -21.8) * mm, "end": v(10.95, -21.8) * mm, "construction": true});
            skLineSegment(sketch, "E120.2.1.13", {"start": v(21.95, -23.8) * mm, "end": v(10.95, -23.8) * mm});
            skLineSegment(sketch, "E120.2.1.14", {"start": v(15.06, -19.8) * mm, "end": v(21.95, -19.8) * mm});
            skLineSegment(sketch, "E120.2.1.15", {"start": v(19.24, -14.49) * mm, "end": v(15.06, -19.8) * mm});
            skArc(sketch, "E120.2.1.16", {"start": v(10.95, -23.8) * mm, "mid": v(9.15, -22.67) * mm, "end": v(9.38, -20.56) * mm});
            skLineSegment(sketch, "E120.2.1.17", {"start": v(14.26, -14.35) * mm, "end": v(11, -10.83) * mm});
            skLineSegment(sketch, "E120.2.1.18", {"start": v(16.05, -8.8) * mm, "end": v(11, -10.83) * mm, "construction": true});
            skLineSegment(sketch, "E120.2.1.19", {"start": v(16.1, -12.02) * mm, "end": v(19.24, -14.49) * mm, "construction": true});
            skLineSegment(sketch, "E120.2.1.20", {"start": v(11.78, -8.17) * mm, "end": v(14.26, -14.35) * mm, "construction": true});
            skArc(sketch, "E120.2.1.21", {"start": v(11, -10.83) * mm, "mid": v(10.21, -9.47) * mm, "end": v(10.24, -7.9) * mm});
            skArc(sketch, "E120.2.1.22", {"start": v(9.2, -5.7) * mm, "mid": v(9.26, -4.58) * mm, "end": v(10.39, -4.63) * mm});
            skArc(sketch, "E120.2.1.23", {"start": v(9.18, -6.37) * mm, "mid": v(8.03, -6.7) * mm, "end": v(8.64, -7.72) * mm});
            skLineSegment(sketch, "E120.2.1.24", {"start": v(16.05, -8.8) * mm, "end": v(16.1, -12.02) * mm});
            skLineSegment(sketch, "E120.2.1.25", {"start": v(20.38, -6.56) * mm, "end": v(23.52, -9.04) * mm, "construction": true});
            skLineSegment(sketch, "E120.2.1.26", {"start": v(13.64, -7.43) * mm, "end": v(15.69, -12.53) * mm, "construction": true});
            skLineSegment(sketch, "E120.2.1.27", {"start": v(15.83, -15.59) * mm, "end": v(12.71, -7.8) * mm, "construction": true});
            skArc(sketch, "E120.2.1.28", {"start": v(14.57, -6.17) * mm, "mid": v(15.67, -7.28) * mm, "end": v(16.05, -8.8) * mm});
            skLineSegment(sketch, "E120.2.1.29", {"start": v(15.69, -12.53) * mm, "end": v(14.26, -14.35) * mm, "construction": true});
            skLineSegment(sketch, "E120.2.1.30", {"start": v(23.52, -9.04) * mm, "end": v(20.38, -6.56) * mm, "construction": true});
            skLineSegment(sketch, "E120.2.1.31", {"start": v(16.1, -12.02) * mm, "end": v(15.69, -12.53) * mm, "construction": true});
            skLineSegment(sketch, "E120.2.1.32", {"start": v(11.44, -6.26) * mm, "end": v(10.39, -4.63) * mm});
            skLineSegment(sketch, "E120.2.1.33", {"start": v(10.39, -4.63) * mm, "end": v(9.2, -5.7) * mm, "construction": true});
            skLineSegment(sketch, "E120.2.1.34", {"start": v(12.71, -7.8) * mm, "end": v(9.5, -4.9) * mm, "construction": true});
            skLineSegment(sketch, "E120.2.1.35", {"start": v(14.57, -6.17) * mm, "end": v(15.6, -4.92) * mm});
            skLineSegment(sketch, "E120.2.1.36", {"start": v(15.6, -4.92) * mm, "end": v(14.28, -4.33) * mm, "construction": true});
            skLineSegment(sketch, "E120.2.1.37", {"start": v(15.02, -4.45) * mm, "end": v(13.08, -8.73) * mm, "construction": true});
            skLineSegment(sketch, "E120.2.1.38", {"start": v(14.03, -5.92) * mm, "end": v(14.28, -4.33) * mm});
            skArc(sketch, "E120.2.1.39", {"start": v(14.03, -5.92) * mm, "mid": v(14.3, -6.03) * mm, "end": v(14.57, -6.17) * mm, "construction": true});
            skArc(sketch, "E120.2.1.40", {"start": v(11.44, -6.26) * mm, "mid": v(12.7, -5.8) * mm, "end": v(14.03, -5.92) * mm});
            skArc(sketch, "E120.2.1.41", {"start": v(14.28, -4.33) * mm, "mid": v(15.33, -3.76) * mm, "end": v(15.6, -4.92) * mm});
            skLineSegment(sketch, "E120.2.1.42", {"start": v(9.2, -5.7) * mm, "end": v(10.78, -6.86) * mm});
            skLineSegment(sketch, "E120.2.1.43", {"start": v(13.64, -7.43) * mm, "end": v(11.78, -8.17) * mm, "construction": true});
            skLineSegment(sketch, "E120.2.1.44", {"start": v(8.64, -7.72) * mm, "end": v(9.18, -6.37) * mm, "construction": true});
            skArc(sketch, "E120.2.1.45", {"start": v(11.78, -8.17) * mm, "mid": v(12.34, -6.87) * mm, "end": v(13.64, -7.43) * mm, "construction": true});
            skLineSegment(sketch, "E120.2.1.46", {"start": v(8.72, -6.97) * mm, "end": v(13.08, -8.73) * mm, "construction": true});
            skLineSegment(sketch, "E120.2.1.47", {"start": v(11.44, -6.26) * mm, "end": v(10.78, -6.86) * mm, "construction": true});
            skLineSegment(sketch, "E120.2.1.48", {"start": v(10.24, -7.9) * mm, "end": v(8.64, -7.72) * mm});
            skArc(sketch, "E120.2.1.49", {"start": v(10.24, -7.9) * mm, "mid": v(10.33, -7.62) * mm, "end": v(10.46, -7.35) * mm, "construction": true});
            skLineSegment(sketch, "E120.2.1.50", {"start": v(10.46, -7.35) * mm, "end": v(9.18, -6.37) * mm});
            skArc(sketch, "E120.2.1.51", {"start": v(10.78, -6.86) * mm, "mid": v(11.09, -6.54) * mm, "end": v(11.44, -6.26) * mm, "construction": true});
            skArc(sketch, "E120.2.1.52", {"start": v(10.46, -7.35) * mm, "mid": v(10.6, -7.1) * mm, "end": v(10.78, -6.86) * mm});
            skLineSegment(sketch, "E120.3.0.0", {"start": v(43.55, 8) * mm, "end": v(54.55, 22) * mm, "construction": true});
            skLineSegment(sketch, "E120.3.0.1", {"start": v(46.86, 15.45) * mm, "end": v(41.98, 9.24) * mm});
            skPoint(sketch, "E120.3.0.2", {"position": v(46.9, 23.77) * mm});
            skPoint(sketch, "E120.3.0.3", {"position": v(47.57, 16.36) * mm});
            skArc(sketch, "E120.3.0.4", {"start": v(52.98, 23.24) * mm, "mid": v(55.79, 23.57) * mm, "end": v(56.12, 20.76) * mm});
            skPoint(sketch, "E120.3.0.5", {"position": v(49.05, 8) * mm});
            skLineSegment(sketch, "E120.3.0.6", {"start": v(56.12, 20.76) * mm, "end": v(47.66, 10) * mm, "construction": true});
            skPoint(sketch, "E120.3.0.7", {"position": v(49.05, 15) * mm});
            skArc(sketch, "E120.3.0.8", {"start": v(54.55, 10) * mm, "mid": v(56.55, 8) * mm, "end": v(54.55, 6) * mm});
            skPoint(sketch, "E120.3.0.9", {"position": v(43.8, 23.36) * mm});
            skLineSegment(sketch, "E120.3.0.10", {"start": v(48.7, 17.78) * mm, "end": v(52.98, 23.24) * mm});
            skLineSegment(sketch, "E120.3.0.11", {"start": v(56.12, 20.76) * mm, "end": v(51.84, 15.31) * mm});
            skLineSegment(sketch, "E120.3.0.12", {"start": v(54.55, 8) * mm, "end": v(43.55, 8) * mm, "construction": true});
            skLineSegment(sketch, "E120.3.0.13", {"start": v(54.55, 6) * mm, "end": v(43.55, 6) * mm});
            skLineSegment(sketch, "E120.3.0.14", {"start": v(47.66, 10) * mm, "end": v(54.55, 10) * mm});
            skLineSegment(sketch, "E120.3.0.15", {"start": v(51.84, 15.31) * mm, "end": v(47.66, 10) * mm});
            skArc(sketch, "E120.3.0.16", {"start": v(43.55, 6) * mm, "mid": v(41.75, 7.13) * mm, "end": v(41.98, 9.24) * mm});
            skLineSegment(sketch, "E120.3.0.17", {"start": v(46.86, 15.45) * mm, "end": v(43.6, 18.97) * mm});
            skLineSegment(sketch, "E120.3.0.18", {"start": v(48.65, 21) * mm, "end": v(43.6, 18.97) * mm, "construction": true});
            skLineSegment(sketch, "E120.3.0.19", {"start": v(48.7, 17.78) * mm, "end": v(51.84, 15.31) * mm, "construction": true});
            skLineSegment(sketch, "E120.3.0.20", {"start": v(44.38, 21.63) * mm, "end": v(46.86, 15.45) * mm, "construction": true});
            skArc(sketch, "E120.3.0.21", {"start": v(43.6, 18.97) * mm, "mid": v(42.81, 20.33) * mm, "end": v(42.84, 21.9) * mm});
            skArc(sketch, "E120.3.0.22", {"start": v(41.8, 24.1) * mm, "mid": v(41.86, 25.22) * mm, "end": v(42.99, 25.17) * mm});
            skArc(sketch, "E120.3.0.23", {"start": v(41.78, 23.43) * mm, "mid": v(40.63, 23.1) * mm, "end": v(41.24, 22.08) * mm});
            skLineSegment(sketch, "E120.3.0.24", {"start": v(48.65, 21) * mm, "end": v(48.7, 17.78) * mm});
            skLineSegment(sketch, "E120.3.0.25", {"start": v(52.98, 23.24) * mm, "end": v(56.12, 20.76) * mm, "construction": true});
            skLineSegment(sketch, "E120.3.0.26", {"start": v(46.24, 22.37) * mm, "end": v(48.29, 17.27) * mm, "construction": true});
            skLineSegment(sketch, "E120.3.0.27", {"start": v(48.43, 14.21) * mm, "end": v(45.31, 22) * mm, "construction": true});
            skArc(sketch, "E120.3.0.28", {"start": v(47.17, 23.63) * mm, "mid": v(48.27, 22.52) * mm, "end": v(48.65, 21) * mm});
            skLineSegment(sketch, "E120.3.0.29", {"start": v(48.29, 17.27) * mm, "end": v(46.86, 15.45) * mm, "construction": true});
            skLineSegment(sketch, "E120.3.0.30", {"start": v(56.12, 20.76) * mm, "end": v(52.98, 23.24) * mm, "construction": true});
            skLineSegment(sketch, "E120.3.0.31", {"start": v(48.7, 17.78) * mm, "end": v(48.29, 17.27) * mm, "construction": true});
            skLineSegment(sketch, "E120.3.0.32", {"start": v(44.04, 23.54) * mm, "end": v(42.99, 25.17) * mm});
            skLineSegment(sketch, "E120.3.0.33", {"start": v(42.99, 25.17) * mm, "end": v(41.8, 24.1) * mm, "construction": true});
            skLineSegment(sketch, "E120.3.0.34", {"start": v(45.31, 22) * mm, "end": v(42.1, 24.9) * mm, "construction": true});
            skLineSegment(sketch, "E120.3.0.35", {"start": v(47.17, 23.63) * mm, "end": v(48.2, 24.88) * mm});
            skLineSegment(sketch, "E120.3.0.36", {"start": v(48.2, 24.88) * mm, "end": v(46.88, 25.47) * mm, "construction": true});
            skLineSegment(sketch, "E120.3.0.37", {"start": v(47.62, 25.35) * mm, "end": v(45.68, 21.07) * mm, "construction": true});
            skLineSegment(sketch, "E120.3.0.38", {"start": v(46.63, 23.88) * mm, "end": v(46.88, 25.47) * mm});
            skArc(sketch, "E120.3.0.39", {"start": v(46.63, 23.88) * mm, "mid": v(46.9, 23.77) * mm, "end": v(47.17, 23.63) * mm, "construction": true});
            skArc(sketch, "E120.3.0.40", {"start": v(44.04, 23.54) * mm, "mid": v(45.3, 24) * mm, "end": v(46.63, 23.88) * mm});
            skArc(sketch, "E120.3.0.41", {"start": v(46.88, 25.47) * mm, "mid": v(47.93, 26.04) * mm, "end": v(48.2, 24.88) * mm});
            skLineSegment(sketch, "E120.3.0.42", {"start": v(41.8, 24.1) * mm, "end": v(43.38, 22.94) * mm});
            skLineSegment(sketch, "E120.3.0.43", {"start": v(46.24, 22.37) * mm, "end": v(44.38, 21.63) * mm, "construction": true});
            skLineSegment(sketch, "E120.3.0.44", {"start": v(41.24, 22.08) * mm, "end": v(41.78, 23.43) * mm, "construction": true});
            skArc(sketch, "E120.3.0.45", {"start": v(44.38, 21.63) * mm, "mid": v(44.94, 22.93) * mm, "end": v(46.24, 22.37) * mm, "construction": true});
            skLineSegment(sketch, "E120.3.0.46", {"start": v(41.32, 22.83) * mm, "end": v(45.68, 21.07) * mm, "construction": true});
            skLineSegment(sketch, "E120.3.0.47", {"start": v(44.04, 23.54) * mm, "end": v(43.38, 22.94) * mm, "construction": true});
            skLineSegment(sketch, "E120.3.0.48", {"start": v(42.84, 21.9) * mm, "end": v(41.24, 22.08) * mm});
            skArc(sketch, "E120.3.0.49", {"start": v(42.84, 21.9) * mm, "mid": v(42.93, 22.18) * mm, "end": v(43.06, 22.45) * mm, "construction": true});
            skLineSegment(sketch, "E120.3.0.50", {"start": v(43.06, 22.45) * mm, "end": v(41.78, 23.43) * mm});
            skArc(sketch, "E120.3.0.51", {"start": v(43.38, 22.94) * mm, "mid": v(43.69, 23.26) * mm, "end": v(44.04, 23.54) * mm, "construction": true});
            skArc(sketch, "E120.3.0.52", {"start": v(43.06, 22.45) * mm, "mid": v(43.2, 22.7) * mm, "end": v(43.38, 22.94) * mm});
            skLineSegment(sketch, "E120.3.1.0", {"start": v(43.55, -21.8) * mm, "end": v(54.55, -7.8) * mm, "construction": true});
            skLineSegment(sketch, "E120.3.1.1", {"start": v(46.86, -14.35) * mm, "end": v(41.98, -20.56) * mm});
            skPoint(sketch, "E120.3.1.2", {"position": v(46.9, -6.03) * mm});
            skPoint(sketch, "E120.3.1.3", {"position": v(47.57, -13.44) * mm});
            skArc(sketch, "E120.3.1.4", {"start": v(52.98, -6.56) * mm, "mid": v(55.79, -6.23) * mm, "end": v(56.12, -9.04) * mm});
            skPoint(sketch, "E120.3.1.5", {"position": v(49.05, -21.8) * mm});
            skLineSegment(sketch, "E120.3.1.6", {"start": v(56.12, -9.04) * mm, "end": v(47.66, -19.8) * mm, "construction": true});
            skPoint(sketch, "E120.3.1.7", {"position": v(49.05, -14.8) * mm});
            skArc(sketch, "E120.3.1.8", {"start": v(54.55, -19.8) * mm, "mid": v(56.55, -21.8) * mm, "end": v(54.55, -23.8) * mm});
            skPoint(sketch, "E120.3.1.9", {"position": v(43.8, -6.44) * mm});
            skLineSegment(sketch, "E120.3.1.10", {"start": v(48.7, -12.02) * mm, "end": v(52.98, -6.56) * mm});
            skLineSegment(sketch, "E120.3.1.11", {"start": v(56.12, -9.04) * mm, "end": v(51.84, -14.49) * mm});
            skLineSegment(sketch, "E120.3.1.12", {"start": v(54.55, -21.8) * mm, "end": v(43.55, -21.8) * mm, "construction": true});
            skLineSegment(sketch, "E120.3.1.13", {"start": v(54.55, -23.8) * mm, "end": v(43.55, -23.8) * mm});
            skLineSegment(sketch, "E120.3.1.14", {"start": v(47.66, -19.8) * mm, "end": v(54.55, -19.8) * mm});
            skLineSegment(sketch, "E120.3.1.15", {"start": v(51.84, -14.49) * mm, "end": v(47.66, -19.8) * mm});
            skArc(sketch, "E120.3.1.16", {"start": v(43.55, -23.8) * mm, "mid": v(41.75, -22.67) * mm, "end": v(41.98, -20.56) * mm});
            skLineSegment(sketch, "E120.3.1.17", {"start": v(46.86, -14.35) * mm, "end": v(43.6, -10.83) * mm});
            skLineSegment(sketch, "E120.3.1.18", {"start": v(48.65, -8.8) * mm, "end": v(43.6, -10.83) * mm, "construction": true});
            skLineSegment(sketch, "E120.3.1.19", {"start": v(48.7, -12.02) * mm, "end": v(51.84, -14.49) * mm, "construction": true});
            skLineSegment(sketch, "E120.3.1.20", {"start": v(44.38, -8.17) * mm, "end": v(46.86, -14.35) * mm, "construction": true});
            skArc(sketch, "E120.3.1.21", {"start": v(43.6, -10.83) * mm, "mid": v(42.81, -9.47) * mm, "end": v(42.84, -7.9) * mm});
            skArc(sketch, "E120.3.1.22", {"start": v(41.8, -5.7) * mm, "mid": v(41.86, -4.58) * mm, "end": v(42.99, -4.63) * mm});
            skArc(sketch, "E120.3.1.23", {"start": v(41.78, -6.37) * mm, "mid": v(40.63, -6.7) * mm, "end": v(41.24, -7.72) * mm});
            skLineSegment(sketch, "E120.3.1.24", {"start": v(48.65, -8.8) * mm, "end": v(48.7, -12.02) * mm});
            skLineSegment(sketch, "E120.3.1.25", {"start": v(52.98, -6.56) * mm, "end": v(56.12, -9.04) * mm, "construction": true});
            skLineSegment(sketch, "E120.3.1.26", {"start": v(46.24, -7.43) * mm, "end": v(48.29, -12.53) * mm, "construction": true});
            skLineSegment(sketch, "E120.3.1.27", {"start": v(48.43, -15.59) * mm, "end": v(45.31, -7.8) * mm, "construction": true});
            skArc(sketch, "E120.3.1.28", {"start": v(47.17, -6.17) * mm, "mid": v(48.27, -7.28) * mm, "end": v(48.65, -8.8) * mm});
            skLineSegment(sketch, "E120.3.1.29", {"start": v(48.29, -12.53) * mm, "end": v(46.86, -14.35) * mm, "construction": true});
            skLineSegment(sketch, "E120.3.1.30", {"start": v(56.12, -9.04) * mm, "end": v(52.98, -6.56) * mm, "construction": true});
            skLineSegment(sketch, "E120.3.1.31", {"start": v(48.7, -12.02) * mm, "end": v(48.29, -12.53) * mm, "construction": true});
            skLineSegment(sketch, "E120.3.1.32", {"start": v(44.04, -6.26) * mm, "end": v(42.99, -4.63) * mm});
            skLineSegment(sketch, "E120.3.1.33", {"start": v(42.99, -4.63) * mm, "end": v(41.8, -5.7) * mm, "construction": true});
            skLineSegment(sketch, "E120.3.1.34", {"start": v(45.31, -7.8) * mm, "end": v(42.1, -4.9) * mm, "construction": true});
            skLineSegment(sketch, "E120.3.1.35", {"start": v(47.17, -6.17) * mm, "end": v(48.2, -4.92) * mm});
            skLineSegment(sketch, "E120.3.1.36", {"start": v(48.2, -4.92) * mm, "end": v(46.88, -4.33) * mm, "construction": true});
            skLineSegment(sketch, "E120.3.1.37", {"start": v(47.62, -4.45) * mm, "end": v(45.68, -8.73) * mm, "construction": true});
            skLineSegment(sketch, "E120.3.1.38", {"start": v(46.63, -5.92) * mm, "end": v(46.88, -4.33) * mm});
            skArc(sketch, "E120.3.1.39", {"start": v(46.63, -5.92) * mm, "mid": v(46.9, -6.03) * mm, "end": v(47.17, -6.17) * mm, "construction": true});
            skArc(sketch, "E120.3.1.40", {"start": v(44.04, -6.26) * mm, "mid": v(45.3, -5.8) * mm, "end": v(46.63, -5.92) * mm});
            skArc(sketch, "E120.3.1.41", {"start": v(46.88, -4.33) * mm, "mid": v(47.93, -3.76) * mm, "end": v(48.2, -4.92) * mm});
            skLineSegment(sketch, "E120.3.1.42", {"start": v(41.8, -5.7) * mm, "end": v(43.38, -6.86) * mm});
            skLineSegment(sketch, "E120.3.1.43", {"start": v(46.24, -7.43) * mm, "end": v(44.38, -8.17) * mm, "construction": true});
            skLineSegment(sketch, "E120.3.1.44", {"start": v(41.24, -7.72) * mm, "end": v(41.78, -6.37) * mm, "construction": true});
            skArc(sketch, "E120.3.1.45", {"start": v(44.38, -8.17) * mm, "mid": v(44.94, -6.87) * mm, "end": v(46.24, -7.43) * mm, "construction": true});
            skLineSegment(sketch, "E120.3.1.46", {"start": v(41.32, -6.97) * mm, "end": v(45.68, -8.73) * mm, "construction": true});
            skLineSegment(sketch, "E120.3.1.47", {"start": v(44.04, -6.26) * mm, "end": v(43.38, -6.86) * mm, "construction": true});
            skLineSegment(sketch, "E120.3.1.48", {"start": v(42.84, -7.9) * mm, "end": v(41.24, -7.72) * mm});
            skArc(sketch, "E120.3.1.49", {"start": v(42.84, -7.9) * mm, "mid": v(42.93, -7.62) * mm, "end": v(43.06, -7.35) * mm, "construction": true});
            skLineSegment(sketch, "E120.3.1.50", {"start": v(43.06, -7.35) * mm, "end": v(41.78, -6.37) * mm});
            skArc(sketch, "E120.3.1.51", {"start": v(43.38, -6.86) * mm, "mid": v(43.69, -6.54) * mm, "end": v(44.04, -6.26) * mm, "construction": true});
            skArc(sketch, "E120.3.1.52", {"start": v(43.06, -7.35) * mm, "mid": v(43.2, -7.1) * mm, "end": v(43.38, -6.86) * mm});
            skLineSegment(sketch, "E120.direction1", {"start": v(-54.25, 6) * mm, "end": v(-21.65, 6) * mm, "construction": true});
            skLineSegment(sketch, "E120.direction2", {"start": v(-54.25, 6) * mm, "end": v(-54.25, -23.8) * mm, "construction": true});
            skSolve(sketch);
        }
        {
            var Q0;
            Q0 = qSketchRegion(id + "F2", true);
            extrude(context, id + "F3", {"entities" : qUnion([Q0]), "operationType" : NewBodyOperationType.REMOVE, "oppositeDirection" : true, "depth" : 13 * mm, "offsetDistance" : 25 * mm, "hasDraft" : true, "draftAngle" : 1 * degree, "draftPullDirection" : true});
        }
        {
            var Q0;
            Q0=makeQuery(id+"F1.opExtrude","CAP_FACE",FACE,{"disambiguationData":[OSD([sQuery(id+"F0.wireOp",EDGE,"E0.bottom"),sQuery(id+"F0.wireOp",EDGE,"E0.top"),sQuery(id+"F0.wireOp",EDGE,"E0.left"),sQuery(id+"F0.wireOp",EDGE,"E0.right"),sQuery(id+"F0.wireOp",EDGE,"E3.filletArc"),sQuery(id+"F0.wireOp",EDGE,"E4.filletArc"),sQuery(id+"F0.wireOp",EDGE,"E5.filletArc"),sQuery(id+"F0.wireOp",EDGE,"E6.filletArc")])],"isStart":false});
            var sketch = newSketch(context, id + "F4", { "sketchPlane" : qUnion([Q0])});
            skLineSegment(sketch, "E121", {"start": v(0, 0) * mm, "end": v(0, 30) * mm, "construction": true});
            skLineSegment(sketch, "E122", {"start": v(-32.5, 15.1) * mm, "end": v(-65, 15.1) * mm, "construction": true});
            skPoint(sketch, "E123", {"position": v(-48.75, 15.1) * mm});
            skArc(sketch, "E124", {"start": v(-35.75, 15.1) * mm, "mid": v(-48.75, 28.1) * mm, "end": v(-61.75, 15.1) * mm});
            skLineSegment(sketch, "E125", {"start": v(-61.75, 15.1) * mm, "end": v(-35.75, 15.1) * mm});
            skArc(sketch, "E126", {"start": v(-61.75, 15.1) * mm, "mid": v(-48.75, 2.1) * mm, "end": v(-35.75, 15.1) * mm, "construction": true});
            skSolve(sketch);
        }
        {
            var Q0;
            Q0 = qSketchRegion(id + "F4", true);
            var Q1;
            Q1=sQuery(id+"F4.wireOp",EDGE,"E122");
            revolve(context, id + "F5", {"operationType" : NewBodyOperationType.REMOVE, "surfaceOperationType" : NewSurfaceOperationType.NEW, "entities" : qUnion([Q0]), "axis" : qUnion([Q1]), "revolveType" : RevolveType.FULL, "oppositeDirection" : true});
        }
        {
            var Q0;
            {var subQ1=sQuery(id+"F4.wireOp",EDGE,"E124");Q0=makeQuery(id+"F4.imprint","IMPRINT",FACE,{"disambiguationData":[TD([[makeQuery(id+"F4.imprint","IMPRINT",EDGE,{"derivedFrom":subQ1}),-1.0]])]});}
            var sketch = newSketch(context, id + "F6", { "sketchPlane" : qUnion([Q0])});
            skPoint(sketch, "E127", {"position": v(-32.84, -0.18) * mm});
            skLineSegment(sketch, "E128", {"start": v(-32.84, -0.18) * mm, "end": v(0, 0) * mm, "construction": true});
            skLineSegment(sketch, "E129", {"start": v(-16.42, -0.09) * mm, "end": v(-16.58, 30) * mm, "construction": true});
            skPoint(sketch, "E130", {"position": v(-16.5, 14.96) * mm});
            skArc(sketch, "E131", {"start": v(-3.5, 15.1) * mm, "mid": v(-16.5, 27.96) * mm, "end": v(-29.5, 15.1) * mm});
            skLineSegment(sketch, "E132", {"start": v(-29.5, 15.1) * mm, "end": v(-3.5, 15.1) * mm});
            skArc(sketch, "E133", {"start": v(-29.5, 15.1) * mm, "mid": v(-16.5, 1.96) * mm, "end": v(-3.5, 15.1) * mm, "construction": true});
            skSolve(sketch);
        }
        {
            var Q0;
            {var subQ1=sQuery(id+"F6.wireOp",EDGE,"E131");Q0=makeQuery(id+"F6.imprint","IMPRINT",FACE,{"disambiguationData":[TD([[makeQuery(id+"F6.imprint","IMPRINT",EDGE,{"derivedFrom":subQ1}),1.0]])]});}
            var Q1;
            Q1=sQuery(id+"F6.wireOp",EDGE,"E132");
            revolve(context, id + "F7", {"operationType" : NewBodyOperationType.REMOVE, "surfaceOperationType" : NewSurfaceOperationType.NEW, "entities" : qUnion([Q0]), "axis" : qUnion([Q1]), "revolveType" : RevolveType.FULL, "oppositeDirection" : true});
        }
        {
            var Q0;
            Q0 = qSketchRegion(id + "F6", true);
            var Q1;
            Q1=sQuery(id+"F4.wireOp",EDGE,"E122");
            revolve(context, id + "F8", {"operationType" : NewBodyOperationType.REMOVE, "surfaceOperationType" : NewSurfaceOperationType.NEW, "entities" : qUnion([Q0]), "axis" : qUnion([Q1]), "revolveType" : RevolveType.FULL});
        }
        {
            var Q0;
            {var subQ1=sQuery(id+"F4.wireOp",EDGE,"E124");Q0=makeQuery(id+"F4.imprint","IMPRINT",FACE,{"disambiguationData":[TD([[makeQuery(id+"F4.imprint","IMPRINT",EDGE,{"derivedFrom":subQ1}),-1.0]])]});}
            var sketch = newSketch(context, id + "F9", { "sketchPlane" : qUnion([Q0])});
            skLineSegment(sketch, "E134", {"start": v(0, 0) * mm, "end": v(0, -30) * mm, "construction": true});
            skLineSegment(sketch, "E135", {"start": v(-65, -15) * mm, "end": v(-32.5, -15) * mm, "construction": true});
            skLineSegment(sketch, "E136", {"start": v(-32.5, -15) * mm, "end": v(0, -15) * mm, "construction": true});
            skArc(sketch, "E137", {"start": v(-35.75, -15) * mm, "mid": v(-48.75, -2) * mm, "end": v(-61.75, -15) * mm});
            skArc(sketch, "E138", {"start": v(-3.25, -15) * mm, "mid": v(-16.25, -2) * mm, "end": v(-29.25, -15) * mm});
            skLineSegment(sketch, "E139", {"start": v(-61.75, -15) * mm, "end": v(-35.75, -15) * mm});
            skLineSegment(sketch, "E140", {"start": v(-29.25, -15) * mm, "end": v(-3.25, -15) * mm});
            skArc(sketch, "E141", {"start": v(-61.75, -15) * mm, "mid": v(-48.75, -28) * mm, "end": v(-35.75, -15) * mm, "construction": true});
            skArc(sketch, "E142", {"start": v(-29.25, -15) * mm, "mid": v(-16.25, -28) * mm, "end": v(-3.25, -15) * mm, "construction": true});
            skSolve(sketch);
        }
        {
            var Q0;
            Q0 = qSketchRegion(id + "F9", true);
            var Q1;
            Q1=sQuery(id+"F9.wireOp",EDGE,"E135");
            revolve(context, id + "F10", {"operationType" : NewBodyOperationType.REMOVE, "surfaceOperationType" : NewSurfaceOperationType.NEW, "entities" : qUnion([Q0]), "axis" : qUnion([Q1]), "revolveType" : RevolveType.FULL, "oppositeDirection" : true});
        }
        {
            var Q0;
            {var subQ1=sQuery(id+"F4.wireOp",EDGE,"E124");Q0=makeQuery(id+"F4.imprint","IMPRINT",FACE,{"disambiguationData":[TD([[makeQuery(id+"F4.imprint","IMPRINT",EDGE,{"derivedFrom":subQ1}),-1.0]])]});}
            var sketch = newSketch(context, id + "F11", { "sketchPlane" : qUnion([Q0])});
            skLineSegment(sketch, "E143", {"start": v(65, 0) * mm, "end": v(32.5, 0) * mm, "construction": true});
            skLineSegment(sketch, "E144", {"start": v(32.5, 0) * mm, "end": v(0, 0) * mm, "construction": true});
            skLineSegment(sketch, "E145", {"start": v(16.25, 30) * mm, "end": v(16.25, 0) * mm, "construction": true});
            skPoint(sketch, "E145.startSnap0", {"position": v(16.25, 0) * mm});
            skLineSegment(sketch, "E146", {"start": v(16.25, 0) * mm, "end": v(16.25, -30) * mm, "construction": true});
            skLineSegment(sketch, "E147", {"start": v(48.75, 0) * mm, "end": v(48.75, 30) * mm, "construction": true});
            skLineSegment(sketch, "E148", {"start": v(48.75, 30) * mm, "end": v(48.75, 0) * mm, "construction": true});
            skLineSegment(sketch, "E149", {"start": v(48.75, 0) * mm, "end": v(48.75, -30) * mm, "construction": true});
            skLineSegment(sketch, "E150.bottom", {"start": v(9.75, 26.5) * mm, "end": v(22.75, 26.5) * mm});
            skLineSegment(sketch, "E150.top", {"start": v(9.75, 3.5) * mm, "end": v(22.75, 3.5) * mm});
            skLineSegment(sketch, "E150.left", {"start": v(4.75, 21.5) * mm, "end": v(4.75, 8.5) * mm});
            skLineSegment(sketch, "E150.right", {"start": v(27.75, 21.5) * mm, "end": v(27.75, 8.5) * mm});
            skPoint(sketch, "E151", {"position": v(16.25, 26.5) * mm});
            skPoint(sketch, "E152", {"position": v(16.25, 15) * mm});
            skPoint(sketch, "E153", {"position": v(4.75, 15) * mm});
            skLineSegment(sketch, "E154.0.1.0", {"start": v(27.75, -8.5) * mm, "end": v(27.75, -26.5) * mm});
            skLineSegment(sketch, "E154.0.1.1", {"start": v(9.75, -3.5) * mm, "end": v(22.75, -3.5) * mm});
            skLineSegment(sketch, "E154.0.1.2", {"start": v(4.75, -8.5) * mm, "end": v(4.75, -21.5) * mm});
            skLineSegment(sketch, "E154.0.1.3", {"start": v(9.75, -26.5) * mm, "end": v(22.75, -26.5) * mm});
            skLineSegment(sketch, "E154.1.0.0", {"start": v(60.25, 21.5) * mm, "end": v(60.25, 8.5) * mm});
            skLineSegment(sketch, "E154.1.0.1", {"start": v(42.25, 26.5) * mm, "end": v(55.25, 26.5) * mm});
            skLineSegment(sketch, "E154.1.0.2", {"start": v(37.25, 21.5) * mm, "end": v(37.25, 8.5) * mm});
            skLineSegment(sketch, "E154.1.0.3", {"start": v(42.25, 3.5) * mm, "end": v(55.25, 3.5) * mm});
            skLineSegment(sketch, "E154.1.1.0", {"start": v(60.25, -8.5) * mm, "end": v(60.25, -21.5) * mm});
            skLineSegment(sketch, "E154.1.1.1", {"start": v(42.25, -3.5) * mm, "end": v(55.25, -3.5) * mm});
            skLineSegment(sketch, "E154.1.1.2", {"start": v(37.25, -8.5) * mm, "end": v(37.25, -21.5) * mm});
            skLineSegment(sketch, "E154.1.1.3", {"start": v(42.25, -26.5) * mm, "end": v(55.25, -26.5) * mm});
            skLineSegment(sketch, "E154.direction1", {"start": v(42.25, 3.5) * mm, "end": v(55.25, 3.5) * mm, "construction": true});
            skLineSegment(sketch, "E154.direction2", {"start": v(27.75, -8.5) * mm, "end": v(27.75, -21.5) * mm, "construction": true});
            skPoint(sketch, "E155.visualSharp", {"position": v(27.75, 26.5) * mm});
            skArc(sketch, "E155.filletArc", {"start": v(27.75, 21.5) * mm, "mid": v(26.29, 25.04) * mm, "end": v(22.75, 26.5) * mm});
            skPoint(sketch, "E156.visualSharp", {"position": v(4.75, 3.5) * mm});
            skArc(sketch, "E156.filletArc", {"start": v(4.75, 8.5) * mm, "mid": v(6.21, 4.96) * mm, "end": v(9.75, 3.5) * mm});
            skPoint(sketch, "E157.visualSharp", {"position": v(4.75, 26.5) * mm});
            skArc(sketch, "E157.filletArc", {"start": v(9.75, 26.5) * mm, "mid": v(6.21, 25.04) * mm, "end": v(4.75, 21.5) * mm});
            skPoint(sketch, "E158.visualSharp", {"position": v(27.75, 3.5) * mm});
            skArc(sketch, "E158.filletArc", {"start": v(22.75, 3.5) * mm, "mid": v(26.29, 4.96) * mm, "end": v(27.75, 8.5) * mm});
            skPoint(sketch, "E159.visualSharp", {"position": v(37.25, 26.5) * mm});
            skArc(sketch, "E159.filletArc", {"start": v(42.25, 26.5) * mm, "mid": v(38.71, 25.04) * mm, "end": v(37.25, 21.5) * mm});
            skPoint(sketch, "E160.visualSharp", {"position": v(60.25, 3.5) * mm});
            skArc(sketch, "E160.filletArc", {"start": v(55.25, 3.5) * mm, "mid": v(58.79, 4.96) * mm, "end": v(60.25, 8.5) * mm});
            skPoint(sketch, "E161.newPointA", {"position": v(37.25, 3.5) * mm});
            skArc(sketch, "E161.filletArc", {"start": v(37.25, 8.5) * mm, "mid": v(38.71, 4.96) * mm, "end": v(42.25, 3.5) * mm});
            skPoint(sketch, "E162.visualSharp", {"position": v(60.25, -3.5) * mm});
            skArc(sketch, "E162.filletArc", {"start": v(60.25, -8.5) * mm, "mid": v(58.79, -4.96) * mm, "end": v(55.25, -3.5) * mm});
            skPoint(sketch, "E163.visualSharp", {"position": v(37.25, -3.5) * mm});
            skArc(sketch, "E163.filletArc", {"start": v(42.25, -3.5) * mm, "mid": v(38.71, -4.96) * mm, "end": v(37.25, -8.5) * mm});
            skPoint(sketch, "E164.visualSharp", {"position": v(60.25, -26.5) * mm});
            skArc(sketch, "E164.filletArc", {"start": v(55.25, -26.5) * mm, "mid": v(58.79, -25.04) * mm, "end": v(60.25, -21.5) * mm});
            skPoint(sketch, "E165.newPointA", {"position": v(27.75, -3.5) * mm});
            skArc(sketch, "E165.filletArc", {"start": v(27.75, -8.5) * mm, "mid": v(26.29, -4.96) * mm, "end": v(22.75, -3.5) * mm});
            skPoint(sketch, "E166.visualSharp", {"position": v(60.25, 26.5) * mm});
            skArc(sketch, "E166.filletArc", {"start": v(60.25, 21.5) * mm, "mid": v(58.79, 25.04) * mm, "end": v(55.25, 26.5) * mm});
            skPoint(sketch, "E167.visualSharp", {"position": v(4.75, -3.5) * mm});
            skArc(sketch, "E167.filletArc", {"start": v(9.75, -3.5) * mm, "mid": v(6.21, -4.96) * mm, "end": v(4.75, -8.5) * mm});
            skPoint(sketch, "E168.visualSharp", {"position": v(27.75, -26.5) * mm});
            skArc(sketch, "E168.filletArc", {"start": v(22.75, -26.5) * mm, "mid": v(26.29, -25.04) * mm, "end": v(27.75, -21.5) * mm});
            skPoint(sketch, "E169.visualSharp", {"position": v(37.25, -26.5) * mm});
            skArc(sketch, "E169.filletArc", {"start": v(37.25, -21.5) * mm, "mid": v(38.71, -25.04) * mm, "end": v(42.25, -26.5) * mm});
            skPoint(sketch, "E170.visualSharp", {"position": v(4.75, -26.5) * mm});
            skArc(sketch, "E170.filletArc", {"start": v(4.75, -21.5) * mm, "mid": v(6.21, -25.04) * mm, "end": v(9.75, -26.5) * mm});
            skSolve(sketch);
        }
        {
            var Q0;
            Q0 = qSketchRegion(id + "F11", true);
            extrude(context, id + "F12", {"entities" : qUnion([Q0]), "operationType" : NewBodyOperationType.REMOVE, "oppositeDirection" : true, "depth" : 7.5 * mm, "offsetDistance" : 25 * mm});
        }
        {
            var Q0;
            Q0=makeQuery(id+"F12.boolean.opBoolean","COPY",EDGE,{"derivedFrom":makeQuery(id+"F12.opExtrude","CAP_EDGE",EDGE,{"disambiguationData":[OSD([sQuery(id+"F11.wireOp",EDGE,"E154.0.1.1")])],"isStart":false})});
            chamfer(context, id + "F13", {"entities" : qUnion([Q0]), "width" : 2 * mm, "tangentPropagation" : true});
        }
        {
            var Q0;
            Q0=makeQuery(id+"F12.boolean.opBoolean","COPY",EDGE,{"derivedFrom":makeQuery(id+"F12.opExtrude","CAP_EDGE",EDGE,{"disambiguationData":[OSD([sQuery(id+"F11.wireOp",EDGE,"E150.right")])],"isStart":false})});
            var Q1;
            Q1=makeQuery(id+"F12.boolean.opBoolean","COPY",EDGE,{"derivedFrom":makeQuery(id+"F12.opExtrude","CAP_EDGE",EDGE,{"disambiguationData":[OSD([sQuery(id+"F11.wireOp",EDGE,"E154.1.0.2")])],"isStart":false})});
            var Q2;
            Q2=makeQuery(id+"F12.boolean.opBoolean","COPY",EDGE,{"derivedFrom":makeQuery(id+"F12.opExtrude","CAP_EDGE",EDGE,{"disambiguationData":[OSD([sQuery(id+"F11.wireOp",EDGE,"E154.1.1.1")])],"isStart":false})});
            chamfer(context, id + "F14", {"entities" : qUnion([Q0, Q1, Q2]), "width" : 2 * mm, "tangentPropagation" : true});
        }
        {
            var Q0;
            Q0=makeQuery(id+"F11.imprint","IMPRINT",FACE,{"disambiguationData":[TD([[makeQuery(id+"F11.imprint","IMPRINT",EDGE,{"derivedFrom":sQuery(id+"F11.wireOp",EDGE,"E150.bottom")}),1.0]])]});
            var sketch = newSketch(context, id + "F15", { "sketchPlane" : qUnion([Q0])});
            skLineSegment(sketch, "E171", {"start": v(-65, 0) * mm, "end": v(0, 0) * mm, "construction": true});
            skLineSegment(sketch, "E172", {"start": v(0, 0) * mm, "end": v(65, 0) * mm, "construction": true});
            skCircle(sketch, "E173.cCircle", {"center": v(-32.5, 0) * mm, "radius": 5 * mm, "construction": true});
            skLineSegment(sketch, "E173.0", {"start": v(-27.5, 2.89) * mm, "end": v(-27.5, -2.89) * mm});
            skLineSegment(sketch, "E173.1", {"start": v(-27.5, -2.89) * mm, "end": v(-32.5, -5.77) * mm});
            skLineSegment(sketch, "E173.2", {"start": v(-32.5, -5.77) * mm, "end": v(-37.5, -2.89) * mm});
            skLineSegment(sketch, "E173.3", {"start": v(-37.5, -2.89) * mm, "end": v(-37.5, 2.89) * mm});
            skLineSegment(sketch, "E173.4", {"start": v(-37.5, 2.89) * mm, "end": v(-32.5, 5.77) * mm});
            skLineSegment(sketch, "E173.5", {"start": v(-32.5, 5.77) * mm, "end": v(-27.5, 2.89) * mm});
            skPoint(sketch, "E173.0.midPoint", {"position": v(-27.5, 0) * mm});
            skCircle(sketch, "E174.cCircle", {"center": v(0, 0) * mm, "radius": 5 * mm, "construction": true});
            skLineSegment(sketch, "E174.0", {"start": v(5, 2.89) * mm, "end": v(5, -2.89) * mm});
            skLineSegment(sketch, "E174.1", {"start": v(5, -2.89) * mm, "end": v(0, -5.77) * mm});
            skLineSegment(sketch, "E174.2", {"start": v(0, -5.77) * mm, "end": v(-5, -2.89) * mm});
            skLineSegment(sketch, "E174.3", {"start": v(-5, -2.89) * mm, "end": v(-5, 2.89) * mm});
            skLineSegment(sketch, "E174.4", {"start": v(-5, 2.89) * mm, "end": v(0, 5.77) * mm});
            skLineSegment(sketch, "E174.5", {"start": v(0, 5.77) * mm, "end": v(5, 2.89) * mm});
            skPoint(sketch, "E174.0.midPoint", {"position": v(5, 0) * mm});
            skCircle(sketch, "E175.cCircle", {"center": v(32.5, 0) * mm, "radius": 5 * mm, "construction": true});
            skLineSegment(sketch, "E175.0", {"start": v(37.5, 2.89) * mm, "end": v(37.5, -2.89) * mm});
            skLineSegment(sketch, "E175.1", {"start": v(37.5, -2.89) * mm, "end": v(32.5, -5.77) * mm});
            skLineSegment(sketch, "E175.2", {"start": v(32.5, -5.77) * mm, "end": v(27.5, -2.89) * mm});
            skLineSegment(sketch, "E175.3", {"start": v(27.5, -2.89) * mm, "end": v(27.5, 2.89) * mm});
            skLineSegment(sketch, "E175.4", {"start": v(27.5, 2.89) * mm, "end": v(32.5, 5.77) * mm});
            skLineSegment(sketch, "E175.5", {"start": v(32.5, 5.77) * mm, "end": v(37.5, 2.89) * mm});
            skPoint(sketch, "E175.0.midPoint", {"position": v(37.5, 0) * mm});
            skSolve(sketch);
        }
        {
            var Q0;
            Q0 = qSketchRegion(id + "F15", true);
            extrude(context, id + "F16", {"entities" : qUnion([Q0]), "operationType" : NewBodyOperationType.REMOVE, "oppositeDirection" : true, "depth" : 25 * mm, "offsetDistance" : 25 * mm});
        }
        {
            var Q0;
            Q0=makeQuery(id+"F0.imprint","IMPRINT",FACE,{"disambiguationData":[TD([[makeQuery(id+"F0.imprint","IMPRINT",EDGE,{"derivedFrom":sQuery(id+"F0.wireOp",EDGE,"E0.bottom")}),-1.0]])]});
            var sketch = newSketch(context, id + "F17", { "sketchPlane" : qUnion([Q0])});
            skLineSegment(sketch, "E176.0", {"start": v(35.25, -8.5) * mm, "end": v(35.25, -30) * mm});
            skArc(sketch, "E176.1", {"start": v(42.25, -1.5) * mm, "mid": v(37.3, -3.55) * mm, "end": v(35.25, -8.5) * mm});
            skLineSegment(sketch, "E176.2", {"start": v(42.25, -1.5) * mm, "end": v(65, -1.5) * mm});
            skLineSegment(sketch, "E177.0", {"start": v(29.75, -8.5) * mm, "end": v(29.75, -30) * mm});
            skArc(sketch, "E177.1", {"start": v(29.75, -8.5) * mm, "mid": v(27.7, -3.55) * mm, "end": v(22.75, -1.5) * mm});
            skLineSegment(sketch, "E177.2", {"start": v(9.75, -1.5) * mm, "end": v(22.75, -1.5) * mm});
            skLineSegment(sketch, "E178.0", {"start": v(42.25, 1.5) * mm, "end": v(65, 1.5) * mm});
            skArc(sketch, "E178.1", {"start": v(35.25, 8.5) * mm, "mid": v(37.3, 3.55) * mm, "end": v(42.25, 1.5) * mm});
            skLineSegment(sketch, "E179.0", {"start": v(29.75, 35.07) * mm, "end": v(29.75, 8.5) * mm});
            skArc(sketch, "E179.1", {"start": v(22.75, 1.5) * mm, "mid": v(27.7, 3.55) * mm, "end": v(29.75, 8.5) * mm});
            skLineSegment(sketch, "E179.2", {"start": v(9.75, 1.5) * mm, "end": v(22.75, 1.5) * mm});
            skLineSegment(sketch, "E180", {"start": v(29.75, -30) * mm, "end": v(35.25, -30) * mm});
            skLineSegment(sketch, "E181", {"start": v(65, -1.5) * mm, "end": v(65, 1.5) * mm});
            skLineSegment(sketch, "E182.0", {"start": v(2.75, -8.5) * mm, "end": v(2.75, -30) * mm});
            skArc(sketch, "E182.1", {"start": v(9.75, -1.5) * mm, "mid": v(4.8, -3.55) * mm, "end": v(2.75, -8.5) * mm});
            skArc(sketch, "E183.0", {"start": v(2.75, 8.5) * mm, "mid": v(4.8, 3.55) * mm, "end": v(9.75, 1.5) * mm});
            skLineSegment(sketch, "E183.1", {"start": v(2.75, 33.74) * mm, "end": v(2.75, 8.5) * mm});
            skArc(sketch, "E184.0", {"start": v(-2.25, -15) * mm, "mid": v(-16.25, -1) * mm, "end": v(-30.25, -15) * mm});
            skArc(sketch, "E185.0", {"start": v(-30.5, 15.1) * mm, "mid": v(-16.5, 0.96) * mm, "end": v(-2.5, 15.1) * mm});
            skArc(sketch, "E186.0", {"start": v(-34.75, -15) * mm, "mid": v(-48.75, -1) * mm, "end": v(-62.75, -15) * mm});
            skArc(sketch, "E187.0", {"start": v(-62.75, 15.1) * mm, "mid": v(-48.75, 1.1) * mm, "end": v(-34.75, 15.1) * mm});
            skLineSegment(sketch, "E188", {"start": v(-34.75, -15) * mm, "end": v(-34.75, -30) * mm});
            skLineSegment(sketch, "E189", {"start": v(-30.25, -15) * mm, "end": v(-30.25, -30) * mm});
            skLineSegment(sketch, "E190", {"start": v(-30.25, -30) * mm, "end": v(-34.75, -30) * mm});
            skLineSegment(sketch, "E191", {"start": v(-2.25, -15) * mm, "end": v(-2.25, -30) * mm});
            skLineSegment(sketch, "E192", {"start": v(-2.25, -30) * mm, "end": v(2.75, -30) * mm});
            skLineSegment(sketch, "E193", {"start": v(-2.5, 15.1) * mm, "end": v(-2.5, 33.74) * mm});
            skLineSegment(sketch, "E194", {"start": v(-30.5, 15.1) * mm, "end": v(-30.31, 33.75) * mm});
            skLineSegment(sketch, "E195", {"start": v(-62.75, -15) * mm, "end": v(-65, -15) * mm});
            skLineSegment(sketch, "E196", {"start": v(-65, -15) * mm, "end": v(-65, 15.1) * mm});
            skLineSegment(sketch, "E197", {"start": v(-65, 15.1) * mm, "end": v(-62.75, 15.1) * mm});
            skLineSegment(sketch, "E198", {"start": v(-34.75, 15.1) * mm, "end": v(-34.75, 33.85) * mm});
            skLineSegment(sketch, "E199", {"start": v(-34.75, 33.85) * mm, "end": v(-30.31, 33.75) * mm});
            skLineSegment(sketch, "E200", {"start": v(-2.5, 33.74) * mm, "end": v(2.75, 33.74) * mm});
            skLineSegment(sketch, "E201", {"start": v(35.25, 8.5) * mm, "end": v(35.25, 34.85) * mm});
            skLineSegment(sketch, "E202", {"start": v(35.25, 34.85) * mm, "end": v(29.75, 35.07) * mm});
            skSolve(sketch);
        }
        {
            var Q0;
            {var subQ0=sQuery(id+"F17.wireOp",EDGE,"E202");Q0=makeQuery(id+"F17.imprint","IMPRINT",FACE,{"disambiguationData":[TD([[makeQuery(id+"F17.imprint","IMPRINT",EDGE,{"derivedFrom":subQ0}),1.0]])]});}
            var Q1;
            {var subQ0=sQuery(id+"F17.wireOp",EDGE,"E200");Q1=makeQuery(id+"F17.imprint","IMPRINT",FACE,{"disambiguationData":[TD([[makeQuery(id+"F17.imprint","IMPRINT",EDGE,{"derivedFrom":subQ0}),-1.0]])]});}
            var Q2;
            {var subQ0=sQuery(id+"F17.wireOp",EDGE,"E199");Q2=makeQuery(id+"F17.imprint","IMPRINT",FACE,{"disambiguationData":[TD([[makeQuery(id+"F17.imprint","IMPRINT",EDGE,{"derivedFrom":subQ0}),-1.0]])]});}
            var Q3;
            Q3=makeQuery(id+"F17.imprint","IMPRINT",FACE,{"disambiguationData":[TD([[makeQuery(id+"F17.imprint","IMPRINT",EDGE,{"derivedFrom":sQuery(id+"F17.wireOp",EDGE,"E176.0")}),-1.0]])]});
            extrude(context, id + "F18", {"entities" : qUnion([Q0, Q1, Q2, Q3]), "operationType" : NewBodyOperationType.REMOVE, "depth" : 10 * mm, "offsetDistance" : 25 * mm});
        }
    });
